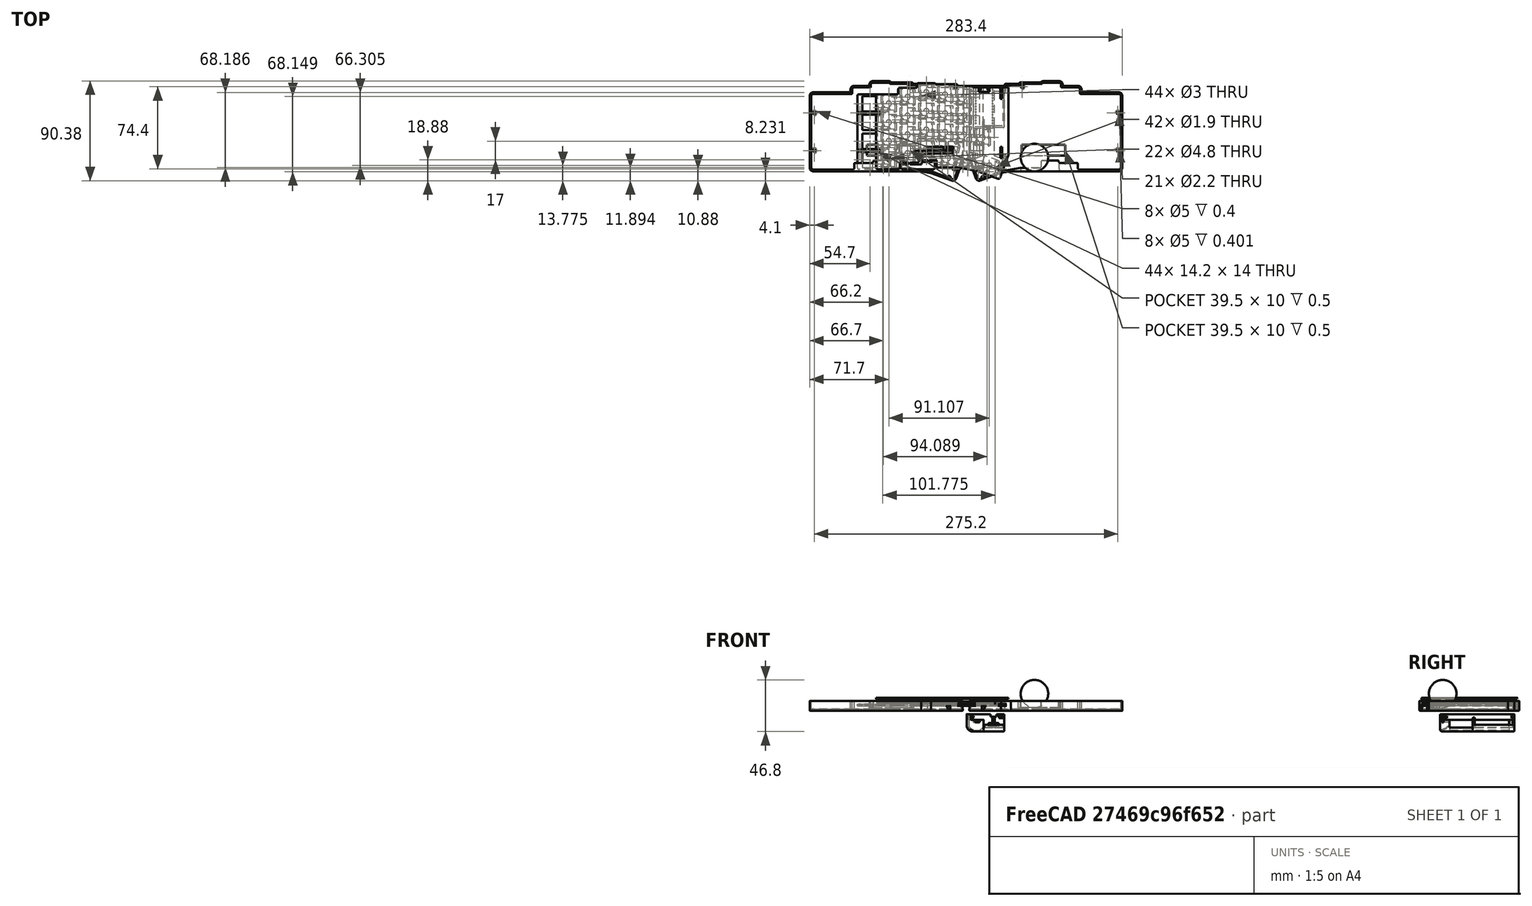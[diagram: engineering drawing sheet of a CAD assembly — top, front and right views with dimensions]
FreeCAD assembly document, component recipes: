
FREECAD ASSEMBLY — COMPONENT RECIPES ("simple-case-MS")

This assembly document has 5 components, labeled P0..P4 below (a component is one placed body or linked part). 4 of them carry a construction recipe — the FreeCAD feature program that regenerates the part from scratch, quoted from this document or its linked companion documents; the rest are supplied as boundary geometry only. No exploded tour is included for this assembly.
NOTE — this tour is split across 3 documents so each fits a 32k-token context. This is document 1: the component sections continue in the remaining 2 documents, each repeating the header above.
COMPONENT P0 — recipe-attached ("Body", modeled in this document).
Construction recipe (the document's own serialized feature program — sketch geometry with constraints, then the solid features built on it; lengths are millimeters unless a unit is written):

FEATURE [Sketcher::SketchObject] Sketch  label="xz"
  ArcFitTolerance = 0
  AttachmentSupport = -> [XZ_Plane]
  ExternalTypes = [0]
  FullyConstrained = false
  MakeInternals = false
  MapMode = 5
  Placement = pos=(0,0,0) rot=(1,0,0;1.5708rad)
  _ExternalGeoVersion = 0
  expr: Constraints[31] = Spreadsheet.conn_h
  expr: Constraints[57] = Spreadsheet.controller_h
  expr: Constraints[79] = Spreadsheet.battery_h
  sketch-geometry (55):
    g0: LineSegment [constr] StartX=9 StartY=2.5 StartZ=0 EndX=9 EndY=4.1 EndZ=0
    g1: LineSegment [constr] StartX=9 StartY=4.1 StartZ=0 EndX=-9 EndY=4.1 EndZ=0
    g2: LineSegment [constr] StartX=-9 StartY=4.1 StartZ=0 EndX=-9 EndY=2.5 EndZ=0
    g3: LineSegment [constr] StartX=-9 StartY=2.5 StartZ=0 EndX=9 EndY=2.5 EndZ=0
    g4: GeomPoint [constr] X=0 Y=3.3 Z=0
    g5: LineSegment [constr] StartX=-105.409 StartY=0 StartZ=0 EndX=45.7381 EndY=0 EndZ=0
    g6: LineSegment [constr] StartX=45.7381 StartY=0 StartZ=0 EndX=45.7381 EndY=-1.6 EndZ=0
    g7: LineSegment [constr] StartX=45.7381 StartY=-1.6 StartZ=0 EndX=-105.409 EndY=-1.6 EndZ=0
    g8: LineSegment [constr] StartX=-105.409 StartY=-1.6 StartZ=0 EndX=-105.409 EndY=0 EndZ=0
    g9: LineSegment [constr] StartX=9 StartY=2.5 StartZ=0 EndX=6.36312 EndY=2.5 EndZ=0
    g10: LineSegment [constr] StartX=6.36312 StartY=2.5 StartZ=0 EndX=6.36312 EndY=0 EndZ=0
    g11: LineSegment [constr] StartX=6.36312 StartY=0 StartZ=0 EndX=9 EndY=0 EndZ=0
    g12: LineSegment [constr] StartX=9 StartY=0 StartZ=0 EndX=9 EndY=2.5 EndZ=0
    g13: LineSegment [constr] StartX=4.55 StartY=-5.1 StartZ=0 EndX=4.55 EndY=-1.6 EndZ=0
    g14: LineSegment [constr] StartX=4.55 StartY=-1.6 StartZ=0 EndX=-4.55 EndY=-1.6 EndZ=0
    g15: LineSegment [constr] StartX=-4.55 StartY=-1.6 StartZ=0 EndX=-4.55 EndY=-5.1 EndZ=0
    g16: LineSegment [constr] StartX=-4.55 StartY=-5.1 StartZ=0 EndX=4.55 EndY=-5.1 EndZ=0
    g17: GeomPoint [constr] X=0 Y=-3.35 Z=0
    g18: LineSegment [constr] StartX=-4.75 StartY=6.3 StartZ=0 EndX=-4.75 EndY=4.1 EndZ=0
    g19: LineSegment [constr] StartX=-4.75 StartY=4.1 StartZ=0 EndX=4.75 EndY=4.1 EndZ=0
    g20: LineSegment [constr] StartX=4.75 StartY=4.1 StartZ=0 EndX=4.75 EndY=6.3 EndZ=0
    g21: LineSegment [constr] StartX=4.75 StartY=6.3 StartZ=0 EndX=-4.75 EndY=6.3 EndZ=0
    g22: GeomPoint [constr] X=0 Y=5.2 Z=0
    g23: LineSegment [constr] StartX=-44.4822 StartY=-5.1 StartZ=0 EndX=-44.4822 EndY=-3.9 EndZ=0
    g24: LineSegment [constr] StartX=-44.4822 StartY=-3.9 StartZ=0 EndX=44.4822 EndY=-3.9 EndZ=0
    g25: LineSegment [constr] StartX=44.4822 StartY=-3.9 StartZ=0 EndX=44.4822 EndY=-5.1 EndZ=0
    g26: LineSegment [constr] StartX=44.4822 StartY=-5.1 StartZ=0 EndX=-44.4822 EndY=-5.1 EndZ=0
    g27: GeomPoint [constr] X=0 Y=-4.5 Z=0
    g28: LineSegment [constr] StartX=-9.1 StartY=-3.6 StartZ=0 EndX=-9.1 EndY=9.4 EndZ=0
    g29: LineSegment [constr] StartX=-9.1 StartY=9.4 StartZ=0 EndX=-22.1 EndY=9.4 EndZ=0
    g30: LineSegment [constr] StartX=-22.1 StartY=9.4 StartZ=0 EndX=-22.1 EndY=-3.6 EndZ=0
    g31: LineSegment [constr] StartX=-22.1 StartY=-3.6 StartZ=0 EndX=-9.1 EndY=-3.6 EndZ=0
    g32: GeomPoint [constr] X=-15.6 Y=2.9 Z=0
    g33: LineSegment [constr] StartX=33.0788 StartY=0.6 StartZ=0 EndX=33.0788 EndY=2.2 EndZ=0
    g34: LineSegment [constr] StartX=33.0788 StartY=2.2 StartZ=0 EndX=11.9844 EndY=2.2 EndZ=0
    g35: LineSegment [constr] StartX=11.9844 StartY=2.2 StartZ=0 EndX=11.9844 EndY=0.6 EndZ=0
    g36: LineSegment [constr] StartX=11.9844 StartY=0.6 StartZ=0 EndX=33.0788 EndY=0.6 EndZ=0
    g37: GeomPoint [constr] X=22.5316 Y=1.4 Z=0
    g38: LineSegment [constr] StartX=25.7428 StartY=8.6 StartZ=0 EndX=25.7428 EndY=2.2 EndZ=0
    g39: LineSegment [constr] StartX=25.7428 StartY=2.2 StartZ=0 EndX=19.3204 EndY=2.2 EndZ=0
    g40: LineSegment [constr] StartX=19.3204 StartY=2.2 StartZ=0 EndX=19.3204 EndY=8.6 EndZ=0
    g41: LineSegment [constr] StartX=19.3204 StartY=8.6 StartZ=0 EndX=25.7428 EndY=8.6 EndZ=0
    g42: GeomPoint [constr] X=22.5316 Y=5.4 Z=0
    g43: LineSegment [constr] StartX=22.5316 StartY=1.4 StartZ=0 EndX=22.5316 EndY=5.4 EndZ=0
    g44: LineSegment [constr] StartX=29.8817 StartY=5.3 StartZ=0 EndX=29.8817 EndY=0 EndZ=0
    g45: LineSegment [constr] StartX=29.8817 StartY=0 StartZ=0 EndX=15.1815 EndY=0 EndZ=0
    g46: LineSegment [constr] StartX=15.1815 StartY=0 StartZ=0 EndX=15.1815 EndY=5.3 EndZ=0
    g47: LineSegment [constr] StartX=15.1815 StartY=5.3 StartZ=0 EndX=29.8817 EndY=5.3 EndZ=0
    g48: GeomPoint [constr] X=22.5316 Y=2.65 Z=0
    g49: LineSegment [constr] StartX=28.1684 StartY=6.59315 StartZ=0 EndX=28.1684 EndY=9.3 EndZ=0
    g50: LineSegment [constr] StartX=28.1684 StartY=9.3 StartZ=0 EndX=16.8947 EndY=9.3 EndZ=0
    g51: LineSegment [constr] StartX=16.8947 StartY=9.3 StartZ=0 EndX=16.8947 EndY=6.59315 EndZ=0
    g52: LineSegment [constr] StartX=16.8947 StartY=6.59315 StartZ=0 EndX=28.1684 EndY=6.59315 EndZ=0
    g53: GeomPoint [constr] X=22.5316 Y=7.94657 Z=0
    g54: Circle [constr] CenterX=41.3382 CenterY=8.9 CenterZ=0 NormalX=0 NormalY=0 NormalZ=1 AngleXU=0 Radius=12.5
  constraints (135):
    c: Coincident(g0,g1)
    c: Coincident(g1,g2)
    c: Coincident(g2,g3)
    c: Coincident(g3,g0)
    c: Horizontal(g1)
    c: Horizontal(g3)
    c: Vertical(g0)
    c: Vertical(g2)
    c: Symmetric(g1,g0,g4)
    c: PointOnObject(g4,g-2)
    c: Coincident(g5,g6)
    c: Coincident(g6,g7)
    c: Coincident(g7,g8)
    c: Coincident(g8,g5)
    c: Horizontal(g5)
    c: Horizontal(g7)
    c: Vertical(g6)
    c: Vertical(g8)
    c: PointOnObject(g5,g-1)
    c: Distance(g6) = 1.6
    c: Distance(g0) = 1.6
    c: Coincident(g9,g10)
    c: Coincident(g10,g11)
    c: Coincident(g11,g12)
    c: Coincident(g12,g9)
    c: Horizontal(g9)
    c: Horizontal(g11)
    c: Vertical(g10)
    c: Vertical(g12)
    c: Coincident(g9,g0)
    c: PointOnObject(g10,g5)
    c: Distance(g12) = 2.5
    c: Distance(g1) = 18
    c: Coincident(g13,g14)
    c: Coincident(g14,g15)
    c: Coincident(g15,g16)
    c: Coincident(g16,g13)
    c: Horizontal(g14)
    c: Horizontal(g16)
    c: Vertical(g13)
    c: Vertical(g15)
    c: Symmetric(g14,g13,g17)
    c: PointOnObject(g17,g-2)
    c: PointOnObject(g14,g7)
    c: Distance(g13) = 3.5
    c: Distance(g16) = 9.1
    c: Coincident(g18,g19)
    c: Coincident(g19,g20)
    c: Coincident(g20,g21)
    c: Coincident(g21,g18)
    c: Horizontal(g19)
    c: Horizontal(g21)
    c: Vertical(g18)
    c: Vertical(g20)
    c: Symmetric(g19,g18,g22)
    c: PointOnObject(g22,g-2)
    c: PointOnObject(g19,g1)
    c: Distance(g20,g3) = 3.8
    c: Distance(g21) = 9.5
    c: Coincident(g23,g24)
    c: Coincident(g24,g25)
    c: Coincident(g25,g26)
    c: Coincident(g26,g23)
    c: Horizontal(g24)
    c: Horizontal(g26)
    c: Vertical(g23)
    c: Vertical(g25)
    c: Symmetric(g24,g23,g27)
    c: PointOnObject(g27,g-2)
    c: Distance(g25) = 1.2
    c: Coincident(g28,g29)
    c: Coincident(g29,g30)
    c: Coincident(g30,g31)
    c: Coincident(g31,g28)
    c: Horizontal(g29)
    c: Horizontal(g31)
    c: Vertical(g28)
    c: Vertical(g30)
    c: Symmetric(g29,g28,g32)
    c: Distance(g30) = 13
    c: Distance(g29) = 13
    c: Distance(g30,g7) = 2
    c: Distance(g24,g7) = 2.3
    c: Distance(g32,g-2) = 15.6
    c: Coincident(g33,g34)
    c: Coincident(g34,g35)
    c: Coincident(g35,g36)
    c: Coincident(g36,g33)
    c: Horizontal(g34)
    c: Horizontal(g36)
    c: Vertical(g33)
    c: Vertical(g35)
    c: Symmetric(g34,g33,g37)
    c: Distance(g33) = 1.6
    c: Distance(g33,g5) = 0.6
    c: Coincident(g38,g39)
    c: Coincident(g39,g40)
    c: Coincident(g40,g41)
    c: Coincident(g41,g38)
    c: Horizontal(g39)
    c: Horizontal(g41)
    c: Vertical(g38)
    c: Vertical(g40)
    c: Symmetric(g39,g38,g42)
    c: PointOnObject(g39,g34)
    c: Distance(g40) = 6.4
    c: Coincident(g43,g37)
    c: Coincident(g43,g42)
    c: Vertical(g43)
    c: Coincident(g44,g45)
    c: Coincident(g45,g46)
    c: Coincident(g46,g47)
    c: Coincident(g47,g44)
    c: Horizontal(g45)
    c: Horizontal(g47)
    c: Vertical(g44)
    c: Vertical(g46)
    c: Symmetric(g45,g44,g48)
    c: PointOnObject(g48,g43)
    c: PointOnObject(g45,g5)
    c: Distance(g44) = 5.3
    c: Coincident(g49,g50)
    c: Coincident(g50,g51)
    c: Coincident(g51,g52)
    c: Coincident(g52,g49)
    c: Horizontal(g50)
    c: Horizontal(g52)
    c: Vertical(g49)
    c: Vertical(g51)
    c: Symmetric(g50,g49,g53)
    c: PointOnObject(g53,g43)
    c: Distance(g49,g47) = 4
    c: Diameter(g54) = 25
    c: Distance(g54,g24) = 12.8
    c: Distance(g33,g24) = 4.5
FEATURE [Sketcher::SketchObject] Sketch001  label="xy"
  ArcFitTolerance = 0
  AttachmentSupport = -> [XY_Plane]
  ExternalTypes = [0]
  FullyConstrained = true
  MakeInternals = false
  MapMode = 5
  _ExternalGeoVersion = 0
  expr: Constraints[23] = Spreadsheet.battery_l
  sketch-geometry (20):
    g0: LineSegment [constr] StartX=8.4 StartY=-34 StartZ=0 EndX=8.4 EndY=0 EndZ=0
    g1: LineSegment [constr] StartX=8.4 StartY=0 StartZ=0 EndX=-8.4 EndY=0 EndZ=0
    g2: LineSegment [constr] StartX=-8.4 StartY=0 StartZ=0 EndX=-8.4 EndY=-34 EndZ=0
    g3: LineSegment [constr] StartX=-8.4 StartY=-34 StartZ=0 EndX=8.4 EndY=-34 EndZ=0
    g4: GeomPoint [constr] X=0 Y=-17 Z=0
    g5: LineSegment [constr] StartX=-22.1 StartY=-60.7 StartZ=0 EndX=-22.1 EndY=-3.7 EndZ=0
    g6: LineSegment [constr] StartX=-22.1 StartY=-3.7 StartZ=0 EndX=-9.1 EndY=-3.7 EndZ=0
    g7: LineSegment [constr] StartX=-9.1 StartY=-3.7 StartZ=0 EndX=-9.1 EndY=-60.7 EndZ=0
    g8: LineSegment [constr] StartX=-9.1 StartY=-60.7 StartZ=0 EndX=-22.1 EndY=-60.7 EndZ=0
    g9: GeomPoint [constr] X=-15.6 Y=-32.2 Z=0
    g10: LineSegment [constr] StartX=22.1 StartY=-68.9 StartZ=0 EndX=22.1 EndY=0 EndZ=0
    g11: LineSegment [constr] StartX=22.1 StartY=0 StartZ=0 EndX=-22.1 EndY=0 EndZ=0
    g12: LineSegment [constr] StartX=-22.1 StartY=0 StartZ=0 EndX=-22.1 EndY=-68.9 EndZ=0
    g13: LineSegment [constr] StartX=-22.1 StartY=-68.9 StartZ=0 EndX=22.1 EndY=-68.9 EndZ=0
    g14: GeomPoint [constr] X=0 Y=-34.45 Z=0
    g15: LineSegment [constr] StartX=8.5 StartY=-53.9 StartZ=0 EndX=8.5 EndY=-36.9 EndZ=0
    g16: LineSegment [constr] StartX=8.5 StartY=-36.9 StartZ=0 EndX=-8.5 EndY=-36.9 EndZ=0
    g17: LineSegment [constr] StartX=-8.5 StartY=-36.9 StartZ=0 EndX=-8.5 EndY=-53.9 EndZ=0
    g18: LineSegment [constr] StartX=-8.5 StartY=-53.9 StartZ=0 EndX=8.5 EndY=-53.9 EndZ=0
    g19: GeomPoint [constr] X=0 Y=-45.4 Z=0
  constraints (52):
    c: Coincident(g0,g1)
    c: Coincident(g1,g2)
    c: Coincident(g2,g3)
    c: Coincident(g3,g0)
    c: Horizontal(g1)
    c: Horizontal(g3)
    c: Vertical(g0)
    c: Vertical(g2)
    c: Symmetric(g1,g0,g4)
    c: PointOnObject(g4,g-2)
    c: Distance(g0) = 34
    c: PointOnObject(g-1,g1)
    c: Distance(g3) = 16.8
    c: Coincident(g5,g6)
    c: Coincident(g6,g7)
    c: Coincident(g7,g8)
    c: Coincident(g8,g5)
    c: Horizontal(g6)
    c: Horizontal(g8)
    c: Vertical(g5)
    c: Vertical(g7)
    c: Symmetric(g6,g5,g9)
    c: Distance(g6) = 13
    c: Distance(g5) = 57
    c: Distance(g9,g-1) = 32.2
    c: Coincident(g10,g11)
    c: Coincident(g11,g12)
    c: Coincident(g12,g13)
    c: Coincident(g13,g10)
    c: Horizontal(g11)
    c: Horizontal(g13)
    c: Vertical(g10)
    c: Vertical(g12)
    c: Symmetric(g11,g10,g14)
    c: PointOnObject(g14,g-2)
    c: PointOnObject(g11,g-1)
    c: Distance(g12,g-2) = 22.1
    c: Distance(g10) = 68.9
    c: Coincident(g15,g16)
    c: Coincident(g16,g17)
    c: Coincident(g17,g18)
    c: Coincident(g18,g15)
    c: Horizontal(g16)
    c: Horizontal(g18)
    c: Vertical(g15)
    c: Vertical(g17)
    c: Symmetric(g16,g15,g19)
    c: PointOnObject(g19,g-2)
    c: Distance(g18) = 17
    c: Distance(g15) = 17
    c: Distance(g19,g-1) = 45.4
    c: Distance(g9,g-2) = 15.6
FEATURE [Sketcher::SketchObject] Sketch002
  ArcFitTolerance = 0
  AttachmentOffset = pos=(0,0,10.6) rot=(0,0,1;0rad)
  AttachmentSupport = -> [XY_Plane]
  ExternalTypes = [0]
  FullyConstrained = true
  MakeInternals = false
  MapMode = 5
  Placement = pos=(0,0,10.6) rot=(0,0,1;0rad)
  _ExternalGeoVersion = 0
  expr: .AttachmentOffset.Base.z = Spreadsheet.battery_h - 3.6 + 1.2
  expr: Constraints[10] = Sketch001.Constraints[10]
  expr: Constraints[12] = Sketch001.Constraints[12]
  expr: Constraints[22] = Sketch001.Constraints[22]
  expr: Constraints[23] = Sketch001.Constraints[23]
  expr: Constraints[24] = Sketch001.Constraints[24]
  expr: Constraints[36] = Sketch001.Constraints[36]
  expr: Constraints[37] = Sketch001.Constraints[37]
  expr: Constraints[48] = Sketch001.Constraints[48]
  expr: Constraints[49] = Sketch001.Constraints[49]
  expr: Constraints[50] = Sketch001.Constraints[50]
  expr: Constraints[51] = Sketch001.Constraints[51]
  sketch-geometry (37):
    g0: LineSegment [constr] StartX=8.4 StartY=-34 StartZ=0 EndX=8.4 EndY=0 EndZ=0
    g1: LineSegment [constr] StartX=8.4 StartY=0 StartZ=0 EndX=-8.4 EndY=0 EndZ=0
    g2: LineSegment [constr] StartX=-8.4 StartY=0 StartZ=0 EndX=-8.4 EndY=-34 EndZ=0
    g3: LineSegment [constr] StartX=-8.4 StartY=-34 StartZ=0 EndX=8.4 EndY=-34 EndZ=0
    g4: GeomPoint [constr] X=0 Y=-17 Z=0
    g5: LineSegment [constr] StartX=-22.1 StartY=-60.7 StartZ=0 EndX=-22.1 EndY=-3.7 EndZ=0
    g6: LineSegment [constr] StartX=-22.1 StartY=-3.7 StartZ=0 EndX=-9.1 EndY=-3.7 EndZ=0
    g7: LineSegment [constr] StartX=-9.1 StartY=-3.7 StartZ=0 EndX=-9.1 EndY=-60.7 EndZ=0
    g8: LineSegment [constr] StartX=-9.1 StartY=-60.7 StartZ=0 EndX=-22.1 EndY=-60.7 EndZ=0
    g9: GeomPoint [constr] X=-15.6 Y=-32.2 Z=0
    g10: LineSegment [constr] StartX=22.1 StartY=-68.9 StartZ=0 EndX=22.1 EndY=0 EndZ=0
    g11: LineSegment [constr] StartX=22.1 StartY=0 StartZ=0 EndX=-22.1 EndY=0 EndZ=0
    g12: LineSegment [constr] StartX=-22.1 StartY=0 StartZ=0 EndX=-22.1 EndY=-68.9 EndZ=0
    g13: LineSegment [constr] StartX=-22.1 StartY=-68.9 StartZ=0 EndX=22.1 EndY=-68.9 EndZ=0
    g14: GeomPoint [constr] X=0 Y=-34.45 Z=0
    g15: LineSegment [constr] StartX=8.5 StartY=-53.9 StartZ=0 EndX=8.5 EndY=-36.9 EndZ=0
    g16: LineSegment [constr] StartX=8.5 StartY=-36.9 StartZ=0 EndX=-8.5 EndY=-36.9 EndZ=0
    g17: LineSegment [constr] StartX=-8.5 StartY=-36.9 StartZ=0 EndX=-8.5 EndY=-53.9 EndZ=0
    g18: LineSegment [constr] StartX=-8.5 StartY=-53.9 StartZ=0 EndX=8.5 EndY=-53.9 EndZ=0
    g19: GeomPoint [constr] X=0 Y=-45.4 Z=0
    g20: LineSegment StartX=9.6 StartY=1.3 StartZ=0 EndX=-24.5 EndY=1.3 EndZ=0
    g21: LineSegment StartX=-24.5 StartY=1.3 StartZ=0 EndX=-24.5 EndY=-1.7 EndZ=0
    g22: LineSegment StartX=-24.5 StartY=-1.7 StartZ=0 EndX=-24.5 EndY=-1.7 EndZ=0
    g23: LineSegment StartX=-24.5 StartY=-1.7 StartZ=0 EndX=-24.5 EndY=-58.7602 EndZ=0
    g24: LineSegment [constr] StartX=-9.1 StartY=-61.6 StartZ=0 EndX=-9.1 EndY=-36.6 EndZ=0
    g25: LineSegment [constr] StartX=-21.7859 StartY=-66.2173 StartZ=0 EndX=-9.1 EndY=-61.6 EndZ=0
    g26: LineSegment StartX=-9.1 StartY=-36.6 StartZ=0 EndX=9.6 EndY=-36.6 EndZ=0
    g27: LineSegment StartX=9.6 StartY=-36.6 StartZ=0 EndX=9.6 EndY=1.3 EndZ=0
    g28: LineSegment StartX=-24.5 StartY=-58.7602 StartZ=0 EndX=-21.7859 EndY=-66.2173 EndZ=0
    g29: LineSegment [constr] StartX=26.9 StartY=-17.32 StartZ=0 EndX=26.9 EndY=-0.32 EndZ=0
    g30: LineSegment [constr] StartX=26.9 StartY=-0.32 StartZ=0 EndX=9.9 EndY=-0.32 EndZ=0
    g31: LineSegment [constr] StartX=9.9 StartY=-0.32 StartZ=0 EndX=9.9 EndY=-17.32 EndZ=0
    g32: LineSegment [constr] StartX=9.9 StartY=-17.32 StartZ=0 EndX=26.9 EndY=-17.32 EndZ=0
    g33: GeomPoint [constr] X=18.4 Y=-8.82 Z=0
    g34: LineSegment StartX=-9.1 StartY=-36.6 StartZ=0 EndX=-9.25 EndY=-36.6 EndZ=0
    g35: LineSegment StartX=-9.25 StartY=-36.6 StartZ=0 EndX=-9.25 EndY=-61.6546 EndZ=0
    g36: LineSegment StartX=-9.25 StartY=-61.6546 StartZ=0 EndX=-21.7859 EndY=-66.2173 EndZ=0
  constraints (100):
    c: Coincident(g0,g1)
    c: Coincident(g1,g2)
    c: Coincident(g2,g3)
    c: Coincident(g3,g0)
    c: Horizontal(g1)
    c: Horizontal(g3)
    c: Vertical(g0)
    c: Vertical(g2)
    c: Symmetric(g1,g0,g4)
    c: PointOnObject(g4,g-2)
    c: Distance(g0) = 34
    c: PointOnObject(g-1,g1)
    c: Distance(g3) = 16.8
    c: Coincident(g5,g6)
    c: Coincident(g6,g7)
    c: Coincident(g7,g8)
    c: Coincident(g8,g5)
    c: Horizontal(g6)
    c: Horizontal(g8)
    c: Vertical(g5)
    c: Vertical(g7)
    c: Symmetric(g6,g5,g9)
    c: Distance(g6) = 13
    c: Distance(g5) = 57
    c: Distance(g9,g-1) = 32.2
    c: Coincident(g10,g11)
    c: Coincident(g11,g12)
    c: Coincident(g12,g13)
    c: Coincident(g13,g10)
    c: Horizontal(g11)
    c: Horizontal(g13)
    c: Vertical(g10)
    c: Vertical(g12)
    c: Symmetric(g11,g10,g14)
    c: PointOnObject(g14,g-2)
    c: PointOnObject(g11,g-1)
    c: Distance(g12,g-2) = 22.1
    c: Distance(g10) = 68.9
    c: Coincident(g15,g16)
    c: Coincident(g16,g17)
    c: Coincident(g17,g18)
    c: Coincident(g18,g15)
    c: Horizontal(g16)
    c: Horizontal(g18)
    c: Vertical(g15)
    c: Vertical(g17)
    c: Symmetric(g16,g15,g19)
    c: PointOnObject(g19,g-2)
    c: Distance(g18) = 17
    c: Distance(g15) = 17
    c: Distance(g19,g-1) = 45.4
    c: Distance(g9,g-2) = 15.6
    c: Horizontal(g20)
    c: Coincident(g21,g20)
    c: Vertical(g21)
    c: Coincident(g22,g21)
    c: Horizontal(g22)
    c: Coincident(g23,g22)
    c: Vertical(g23)
    c: PointOnObject(g24,g7)
    c: Vertical(g24)
    c: Distance(g11,g21) = 2.4
    c: Distance(g21,g6) = 2
    c: Distance(g22,g5) = 2.4
    c: Coincident(g24,g25)
    c: Angle(g13,g25) = 0.349066
    c: DistanceY(g-1,g20) = 1.3
    c: Coincident(g26,g24)
    c: Horizontal(g26)
    c: Coincident(g27,g26)
    c: Coincident(g27,g20)
    c: Vertical(g27)
    c: Distance(g15,g26) = 0.3
    c: Coincident(g28,g23)
    c: Coincident(g28,g25)
    c: Distance(g25,g25) = 13.5
    c: Perpendicular(g28,g25)
    c: Distance(g24,g8) = 0.9
    c: Coincident(g29,g30)
    c: Coincident(g30,g31)
    c: Coincident(g31,g32)
    c: Coincident(g32,g29)
    c: Vertical(g29)
    c: Vertical(g31)
    c: Horizontal(g30)
    c: Horizontal(g32)
    c: Symmetric(g31,g29,g33)
    c: DistanceX(g30,g30) = 17
    c: DistanceY(g29,g29) = 17
    c: DistanceX(g-1,g33) = 18.4
    c: DistanceY(g33,g-1) = 8.82
    c: Distance(g31,g27) = 0.3
    c: Coincident(g24,g34)
    c: Horizontal(g34)
    c: Coincident(g34,g35)
    c: PointOnObject(g35,g25)
    c: Vertical(g35)
    c: Coincident(g35,g36)
    c: Coincident(g36,g25)
    c: Distance(g35,g7) = 0.15
FEATURE [PartDesign::Pad] Pad  label="ベース"
  Direction = (0,0,1)
  Length = 15.7
  Length2 = 10
  Profile = -> Sketch002
  ReferenceAxis = -> Sketch002 [N_Axis]
  Reversed = true
  SideType = 0
  Suppressed = false
  Type = 0
  Type2 = 0
  expr: Length = Spreadsheet.battery_h + 1.2 + 0.3 + 1.2
FEATURE [Sketcher::SketchObject] Sketch003
  ArcFitTolerance = 0
  AttachmentOffset = pos=(0,0,6.9) rot=(0,0,1;0rad)
  AttachmentSupport = -> [XY_Plane]
  ExternalTypes = [0]
  FullyConstrained = false
  MakeInternals = false
  MapMode = 5
  Placement = pos=(0,0,6.9) rot=(0,0,1;0rad)
  _ExternalGeoVersion = 0
  expr: .AttachmentOffset.Base.z = Spreadsheet.conn_h + Spreadsheet.controller_h + 0.6
  expr: Constraints[10] = Sketch001.Constraints[10]
  expr: Constraints[12] = Sketch001.Constraints[12]
  expr: Constraints[22] = Sketch001.Constraints[22]
  expr: Constraints[23] = Sketch001.Constraints[23]
  expr: Constraints[24] = Sketch001.Constraints[24]
  expr: Constraints[36] = Sketch001.Constraints[36]
  expr: Constraints[37] = Sketch001.Constraints[37]
  expr: Constraints[48] = Sketch001.Constraints[48]
  expr: Constraints[49] = Sketch001.Constraints[49]
  expr: Constraints[50] = Sketch001.Constraints[50]
  expr: Constraints[51] = Sketch001.Constraints[51]
  sketch-geometry (24):
    g0: LineSegment [constr] StartX=8.4 StartY=-34 StartZ=0 EndX=8.4 EndY=0 EndZ=0
    g1: LineSegment [constr] StartX=8.4 StartY=0 StartZ=0 EndX=-8.4 EndY=0 EndZ=0
    g2: LineSegment [constr] StartX=-8.4 StartY=0 StartZ=0 EndX=-8.4 EndY=-34 EndZ=0
    g3: LineSegment [constr] StartX=-8.4 StartY=-34 StartZ=0 EndX=8.4 EndY=-34 EndZ=0
    g4: GeomPoint [constr] X=0 Y=-17 Z=0
    g5: LineSegment [constr] StartX=-22.1 StartY=-60.7 StartZ=0 EndX=-22.1 EndY=-3.7 EndZ=0
    g6: LineSegment [constr] StartX=-22.1 StartY=-3.7 StartZ=0 EndX=-9.1 EndY=-3.7 EndZ=0
    g7: LineSegment [constr] StartX=-9.1 StartY=-3.7 StartZ=0 EndX=-9.1 EndY=-60.7 EndZ=0
    g8: LineSegment [constr] StartX=-9.1 StartY=-60.7 StartZ=0 EndX=-22.1 EndY=-60.7 EndZ=0
    g9: GeomPoint [constr] X=-15.6 Y=-32.2 Z=0
    g10: LineSegment [constr] StartX=22.1 StartY=-68.9 StartZ=0 EndX=22.1 EndY=0 EndZ=0
    g11: LineSegment [constr] StartX=22.1 StartY=0 StartZ=0 EndX=-22.1 EndY=0 EndZ=0
    g12: LineSegment [constr] StartX=-22.1 StartY=0 StartZ=0 EndX=-22.1 EndY=-68.9 EndZ=0
    g13: LineSegment [constr] StartX=-22.1 StartY=-68.9 StartZ=0 EndX=22.1 EndY=-68.9 EndZ=0
    g14: GeomPoint [constr] X=0 Y=-34.45 Z=0
    g15: LineSegment [constr] StartX=8.5 StartY=-53.9 StartZ=0 EndX=8.5 EndY=-36.9 EndZ=0
    g16: LineSegment [constr] StartX=8.5 StartY=-36.9 StartZ=0 EndX=-8.5 EndY=-36.9 EndZ=0
    g17: LineSegment [constr] StartX=-8.5 StartY=-36.9 StartZ=0 EndX=-8.5 EndY=-53.9 EndZ=0
    g18: LineSegment [constr] StartX=-8.5 StartY=-53.9 StartZ=0 EndX=8.5 EndY=-53.9 EndZ=0
    g19: GeomPoint [constr] X=0 Y=-45.4 Z=0
    g20: LineSegment StartX=8.4 StartY=0 StartZ=0 EndX=-9.1 EndY=0 EndZ=0
    g21: LineSegment StartX=-9.1 StartY=0 StartZ=0 EndX=-9.1 EndY=-40.6656 EndZ=0
    g22: LineSegment StartX=-9.1 StartY=-40.6656 StartZ=0 EndX=8.4 EndY=-40.6656 EndZ=0
    g23: LineSegment StartX=8.4 StartY=-40.6656 StartZ=0 EndX=8.4 EndY=0 EndZ=0
  constraints (62):
    c: Coincident(g0,g1)
    c: Coincident(g1,g2)
    c: Coincident(g2,g3)
    c: Coincident(g3,g0)
    c: Horizontal(g1)
    c: Horizontal(g3)
    c: Vertical(g0)
    c: Vertical(g2)
    c: Symmetric(g1,g0,g4)
    c: PointOnObject(g4,g-2)
    c: Distance(g0) = 34
    c: PointOnObject(g-1,g1)
    c: Distance(g3) = 16.8
    c: Coincident(g5,g6)
    c: Coincident(g6,g7)
    c: Coincident(g7,g8)
    c: Coincident(g8,g5)
    c: Horizontal(g6)
    c: Horizontal(g8)
    c: Vertical(g5)
    c: Vertical(g7)
    c: Symmetric(g6,g5,g9)
    c: Distance(g6) = 13
    c: Distance(g5) = 57
    c: Distance(g9,g-1) = 32.2
    c: Coincident(g10,g11)
    c: Coincident(g11,g12)
    c: Coincident(g12,g13)
    c: Coincident(g13,g10)
    c: Horizontal(g11)
    c: Horizontal(g13)
    c: Vertical(g10)
    c: Vertical(g12)
    c: Symmetric(g11,g10,g14)
    c: PointOnObject(g14,g-2)
    c: PointOnObject(g11,g-1)
    c: Distance(g12,g-2) = 22.1
    c: Distance(g10) = 68.9
    c: Coincident(g15,g16)
    c: Coincident(g16,g17)
    c: Coincident(g17,g18)
    c: Coincident(g18,g15)
    c: Horizontal(g16)
    c: Horizontal(g18)
    c: Vertical(g15)
    c: Vertical(g17)
    c: Symmetric(g16,g15,g19)
    c: PointOnObject(g19,g-2)
    c: Distance(g18) = 17
    c: Distance(g15) = 17
    c: Distance(g19,g-1) = 45.4
    c: Distance(g9,g-2) = 15.6
    c: Coincident(g20,g21)
    c: Coincident(g21,g22)
    c: Coincident(g22,g23)
    c: Coincident(g23,g20)
    c: Horizontal(g20)
    c: Horizontal(g22)
    c: Vertical(g21)
    c: Vertical(g23)
    c: Coincident(g20,g0)
    c: PointOnObject(g21,g7)
FEATURE [PartDesign::Pocket] Pocket  label="コントローラ部"
  BaseFeature = -> Pad
  Direction = (0,0,-1)
  Length = 5
  Length2 = 5
  Profile = -> Sketch003
  ReferenceAxis = -> Sketch003 [N_Axis]
  SideType = 0
  Suppressed = false
  Type = 1
  Type2 = 0
FEATURE [Sketcher::SketchObject] Sketch007
  ArcFitTolerance = 0
  AttachmentSupport = -> [XY_Plane]
  ExternalTypes = [0]
  FullyConstrained = false
  MakeInternals = false
  MapMode = 5
  _ExternalGeoVersion = 0
  expr: Constraints[10] = Sketch001.Constraints[10]
  expr: Constraints[12] = Sketch001.Constraints[12]
  expr: Constraints[21] = Sketch001.Constraints[22]
  expr: Constraints[22] = Sketch001.Constraints[23]
  expr: Constraints[23] = Sketch001.Constraints[24]
  expr: Constraints[35] = Sketch001.Constraints[36]
  expr: Constraints[36] = Sketch001.Constraints[37]
  expr: Constraints[47] = Sketch001.Constraints[48]
  expr: Constraints[48] = Sketch001.Constraints[49]
  expr: Constraints[49] = Sketch001.Constraints[50]
  expr: Constraints[50] = Sketch001.Constraints[51]
  sketch-geometry (28):
    g0: LineSegment [constr] StartX=8.4 StartY=-34 StartZ=0 EndX=8.4 EndY=0 EndZ=0
    g1: LineSegment [constr] StartX=8.4 StartY=0 StartZ=0 EndX=-8.4 EndY=0 EndZ=0
    g2: LineSegment [constr] StartX=-8.4 StartY=0 StartZ=0 EndX=-8.4 EndY=-34 EndZ=0
    g3: LineSegment [constr] StartX=-8.4 StartY=-34 StartZ=0 EndX=8.4 EndY=-34 EndZ=0
    g4: GeomPoint [constr] X=0 Y=-17 Z=0
    g5: LineSegment [constr] StartX=-22.1 StartY=-60.7 StartZ=0 EndX=-22.1 EndY=-3.7 EndZ=0
    g6: LineSegment [constr] StartX=-22.1 StartY=-3.7 StartZ=0 EndX=-9.1 EndY=-3.7 EndZ=0
    g7: LineSegment [constr] StartX=-9.1 StartY=-3.7 StartZ=0 EndX=-9.1 EndY=-60.7 EndZ=0
    g8: LineSegment [constr] StartX=-9.1 StartY=-60.7 StartZ=0 EndX=-22.1 EndY=-60.7 EndZ=0
    g9: GeomPoint [constr] X=-15.6 Y=-32.2 Z=0
    g10: LineSegment [constr] StartX=22.1 StartY=-68.9 StartZ=0 EndX=22.1 EndY=0 EndZ=0
    g11: LineSegment [constr] StartX=22.1 StartY=0 StartZ=0 EndX=-22.1 EndY=0 EndZ=0
    g12: LineSegment [constr] StartX=-22.1 StartY=0 StartZ=0 EndX=-22.1 EndY=-68.9 EndZ=0
    g13: LineSegment [constr] StartX=-22.1 StartY=-68.9 StartZ=0 EndX=22.1 EndY=-68.9 EndZ=0
    g14: GeomPoint [constr] X=0 Y=-34.45 Z=0
    g15: LineSegment [constr] StartX=8.5 StartY=-53.9 StartZ=0 EndX=8.5 EndY=-36.9 EndZ=0
    g16: LineSegment [constr] StartX=8.5 StartY=-36.9 StartZ=0 EndX=-8.5 EndY=-36.9 EndZ=0
    g17: LineSegment [constr] StartX=-8.5 StartY=-36.9 StartZ=0 EndX=-8.5 EndY=-53.9 EndZ=0
    g18: LineSegment [constr] StartX=-8.5 StartY=-53.9 StartZ=0 EndX=8.5 EndY=-53.9 EndZ=0
    g19: GeomPoint [constr] X=-1.4e-15 Y=-45.4 Z=0
    g20: LineSegment StartX=22.1 StartY=0 StartZ=0 EndX=-22.4 EndY=0 EndZ=0
    g21: LineSegment StartX=-22.4 StartY=0 StartZ=0 EndX=-22.4 EndY=-4 EndZ=0
    g22: LineSegment StartX=-22.4 StartY=-4 StartZ=0 EndX=-22.4 EndY=-60.9323 EndZ=0
    g23: LineSegment [constr] StartX=-22.4 StartY=-60.4 StartZ=0 EndX=-22.4 EndY=-68.9 EndZ=0
    g24: LineSegment [constr] StartX=-22.4 StartY=-68.9 StartZ=0 EndX=22.1 EndY=-68.9 EndZ=0
    g25: LineSegment StartX=22.1 StartY=-68.9 StartZ=0 EndX=22.1 EndY=0 EndZ=0
    g26: LineSegment StartX=-19.5 StartY=-68.9 StartZ=0 EndX=22.1 EndY=-68.9 EndZ=0
    g27: LineSegment StartX=-22.4 StartY=-60.9323 StartZ=0 EndX=-19.5 EndY=-68.9 EndZ=0
  constraints (71):
    c: Coincident(g0,g1)
    c: Coincident(g1,g2)
    c: Coincident(g2,g3)
    c: Coincident(g3,g0)
    c: Horizontal(g1)
    c: Horizontal(g3)
    c: Vertical(g0)
    c: Vertical(g2)
    c: Symmetric(g1,g0,g4)
    c: PointOnObject(g4,g-2)
    c: Distance(g0) = 34
    c: PointOnObject(g-1,g1)
    c: Distance(g3) = 16.8
    c: Coincident(g5,g6)
    c: Coincident(g6,g7)
    c: Coincident(g7,g8)
    c: Horizontal(g6)
    c: Horizontal(g8)
    c: Vertical(g5)
    c: Vertical(g7)
    c: Symmetric(g6,g5,g9)
    c: Distance(g6) = 13
    c: Distance(g5) = 57
    c: Distance(g9,g-1) = 32.2
    c: Coincident(g10,g11)
    c: Coincident(g11,g12)
    c: Coincident(g12,g13)
    c: Coincident(g13,g10)
    c: Horizontal(g11)
    c: Horizontal(g13)
    c: Vertical(g10)
    c: Vertical(g12)
    c: Symmetric(g11,g10,g14)
    c: PointOnObject(g14,g-2)
    c: PointOnObject(g11,g-1)
    c: Distance(g12,g-2) = 22.1
    c: Distance(g10) = 68.9
    c: Coincident(g15,g16)
    c: Coincident(g16,g17)
    c: Coincident(g17,g18)
    c: Coincident(g18,g15)
    c: Horizontal(g16)
    c: Horizontal(g18)
    c: Vertical(g15)
    c: Vertical(g17)
    c: Symmetric(g16,g15,g19)
    c: PointOnObject(g19,g-2)
    c: Distance(g18) = 17
    c: Distance(g15) = 17
    c: Distance(g19,g-1) = 45.4
    c: Distance(g9,g-2) = 15.6
    c: Coincident(g20,g10)
    c: PointOnObject(g20,g-1)
    c: Coincident(g21,g20)
    c: Vertical(g21)
    c: Vertical(g22)
    c: Vertical(g23)
    c: Coincident(g24,g23)
    c: Coincident(g24,g10)
    c: Horizontal(g24)
    c: Coincident(g25,g24)
    c: Coincident(g25,g20)
    c: Distance(g21,g12) = 0.3
    c: Distance(g21,g6) = 0.3
    c: PointOnObject(g26,g13)
    c: Coincident(g26,g10)
    c: Coincident(g27,g22)
    c: Coincident(g27,g26)
    c: Angle(g26,g27) = 1.91986
    c: DistanceX(g27,g27) = 2.9
    c: Coincident(g22,g21)
FEATURE [PartDesign::Pocket] Pocket001  label="基板部"
  BaseFeature = -> Pocket
  Direction = (0,0,-1)
  Length = 5
  Length2 = 5
  Profile = -> Sketch007
  ReferenceAxis = -> Sketch007 [N_Axis]
  SideType = 0
  Suppressed = false
  Type = 1
  Type2 = 0
FEATURE [Sketcher::SketchObject] Sketch008
  ArcFitTolerance = 0
  AttachmentOffset = pos=(0,0,3.4) rot=(0,0,1;0rad)
  AttachmentSupport = -> [XZ_Plane]
  ExternalTypes = [0]
  FullyConstrained = false
  MakeInternals = false
  MapMode = 5
  Placement = pos=(0,-3.4,8e-16) rot=(1,0,0;1.5708rad)
  _ExternalGeoVersion = 0
  expr: Constraints[105] = Sketch.Constraints[105]
  expr: Constraints[120] = Sketch.Constraints[120]
  expr: Constraints[131] = Sketch.Constraints[131]
  expr: Constraints[132] = Sketch.Constraints[132]
  expr: Constraints[133] = Sketch.Constraints[133]
  expr: Constraints[19] = Sketch.Constraints[19]
  expr: Constraints[20] = Sketch.Constraints[20]
  expr: Constraints[31] = Sketch.Constraints[31]
  expr: Constraints[32] = Sketch.Constraints[32]
  expr: Constraints[44] = Sketch.Constraints[44]
  expr: Constraints[45] = Sketch.Constraints[45]
  expr: Constraints[57] = Sketch.Constraints[57]
  expr: Constraints[58] = Sketch.Constraints[58]
  expr: Constraints[69] = Sketch.Constraints[69]
  expr: Constraints[79] = Sketch.Constraints[79]
  expr: Constraints[80] = Sketch.Constraints[80]
  expr: Constraints[81] = Sketch.Constraints[81]
  expr: Constraints[82] = Sketch.Constraints[82]
  expr: Constraints[83] = Sketch.Constraints[83]
  expr: Constraints[93] = Sketch.Constraints[93]
  expr: Constraints[94] = Sketch.Constraints[94]
  sketch-geometry (70):
    g0: LineSegment [constr] StartX=9 StartY=2.5 StartZ=0 EndX=9 EndY=4.1 EndZ=0
    g1: LineSegment [constr] StartX=9 StartY=4.1 StartZ=0 EndX=-9 EndY=4.1 EndZ=0
    g2: LineSegment [constr] StartX=-9 StartY=4.1 StartZ=0 EndX=-9 EndY=2.5 EndZ=0
    g3: LineSegment [constr] StartX=-9 StartY=2.5 StartZ=0 EndX=9 EndY=2.5 EndZ=0
    g4: GeomPoint [constr] X=0 Y=3.3 Z=0
    g5: LineSegment [constr] StartX=-105.409 StartY=0 StartZ=0 EndX=45.7381 EndY=0 EndZ=0
    g6: LineSegment [constr] StartX=45.7381 StartY=0 StartZ=0 EndX=45.7381 EndY=-1.6 EndZ=0
    g7: LineSegment [constr] StartX=45.7381 StartY=-1.6 StartZ=0 EndX=-105.409 EndY=-1.6 EndZ=0
    g8: LineSegment [constr] StartX=-105.409 StartY=-1.6 StartZ=0 EndX=-105.409 EndY=0 EndZ=0
    g9: LineSegment [constr] StartX=9 StartY=2.5 StartZ=0 EndX=6.36312 EndY=2.5 EndZ=0
    g10: LineSegment [constr] StartX=6.36312 StartY=2.5 StartZ=0 EndX=6.36312 EndY=0 EndZ=0
    g11: LineSegment [constr] StartX=6.36312 StartY=0 StartZ=0 EndX=9 EndY=0 EndZ=0
    g12: LineSegment [constr] StartX=9 StartY=0 StartZ=0 EndX=9 EndY=2.5 EndZ=0
    g13: LineSegment [constr] StartX=4.55 StartY=-5.1 StartZ=0 EndX=4.55 EndY=-1.6 EndZ=0
    g14: LineSegment [constr] StartX=4.55 StartY=-1.6 StartZ=0 EndX=-4.55 EndY=-1.6 EndZ=0
    g15: LineSegment [constr] StartX=-4.55 StartY=-1.6 StartZ=0 EndX=-4.55 EndY=-5.1 EndZ=0
    g16: LineSegment [constr] StartX=-4.55 StartY=-5.1 StartZ=0 EndX=4.55 EndY=-5.1 EndZ=0
    g17: GeomPoint [constr] X=0 Y=-3.35 Z=0
    g18: LineSegment [constr] StartX=-4.75 StartY=6.3 StartZ=0 EndX=-4.75 EndY=4.1 EndZ=0
    g19: LineSegment [constr] StartX=-4.75 StartY=4.1 StartZ=0 EndX=4.75 EndY=4.1 EndZ=0
    g20: LineSegment [constr] StartX=4.75 StartY=4.1 StartZ=0 EndX=4.75 EndY=6.3 EndZ=0
    g21: LineSegment [constr] StartX=4.75 StartY=6.3 StartZ=0 EndX=-4.75 EndY=6.3 EndZ=0
    g22: GeomPoint [constr] X=0 Y=5.2 Z=0
    g23: LineSegment [constr] StartX=-44.4822 StartY=-5.1 StartZ=0 EndX=-44.4822 EndY=-3.9 EndZ=0
    g24: LineSegment [constr] StartX=-44.4822 StartY=-3.9 StartZ=0 EndX=44.4822 EndY=-3.9 EndZ=0
    g25: LineSegment [constr] StartX=44.4822 StartY=-3.9 StartZ=0 EndX=44.4822 EndY=-5.1 EndZ=0
    g26: LineSegment [constr] StartX=44.4822 StartY=-5.1 StartZ=0 EndX=-44.4822 EndY=-5.1 EndZ=0
    g27: GeomPoint [constr] X=0 Y=-4.5 Z=0
    g28: LineSegment [constr] StartX=-9.1 StartY=-3.6 StartZ=0 EndX=-9.1 EndY=9.4 EndZ=0
    g29: LineSegment [constr] StartX=-9.1 StartY=9.4 StartZ=0 EndX=-22.1 EndY=9.4 EndZ=0
    g30: LineSegment [constr] StartX=-22.1 StartY=9.4 StartZ=0 EndX=-22.1 EndY=-3.6 EndZ=0
    g31: LineSegment [constr] StartX=-22.1 StartY=-3.6 StartZ=0 EndX=-9.1 EndY=-3.6 EndZ=0
    g32: GeomPoint [constr] X=-15.6 Y=2.9 Z=0
    g33: LineSegment [constr] StartX=33.0788 StartY=0.6 StartZ=0 EndX=33.0788 EndY=2.2 EndZ=0
    g34: LineSegment [constr] StartX=33.0788 StartY=2.2 StartZ=0 EndX=11.9844 EndY=2.2 EndZ=0
    g35: LineSegment [constr] StartX=11.9844 StartY=2.2 StartZ=0 EndX=11.9844 EndY=0.6 EndZ=0
    g36: LineSegment [constr] StartX=11.9844 StartY=0.6 StartZ=0 EndX=33.0788 EndY=0.6 EndZ=0
    g37: GeomPoint [constr] X=22.5316 Y=1.4 Z=0
    g38: LineSegment [constr] StartX=25.7428 StartY=8.6 StartZ=0 EndX=25.7428 EndY=2.2 EndZ=0
    g39: LineSegment [constr] StartX=25.7428 StartY=2.2 StartZ=0 EndX=19.3204 EndY=2.2 EndZ=0
    g40: LineSegment [constr] StartX=19.3204 StartY=2.2 StartZ=0 EndX=19.3204 EndY=8.6 EndZ=0
    g41: LineSegment [constr] StartX=19.3204 StartY=8.6 StartZ=0 EndX=25.7428 EndY=8.6 EndZ=0
    g42: GeomPoint [constr] X=22.5316 Y=5.4 Z=0
    g43: LineSegment [constr] StartX=22.5316 StartY=1.4 StartZ=0 EndX=22.5316 EndY=5.4 EndZ=0
    g44: LineSegment [constr] StartX=29.8817 StartY=5.3 StartZ=0 EndX=29.8817 EndY=0 EndZ=0
    g45: LineSegment [constr] StartX=29.8817 StartY=0 StartZ=0 EndX=15.1815 EndY=0 EndZ=0
    g46: LineSegment [constr] StartX=15.1815 StartY=0 StartZ=0 EndX=15.1815 EndY=5.3 EndZ=0
    g47: LineSegment [constr] StartX=15.1815 StartY=5.3 StartZ=0 EndX=29.8817 EndY=5.3 EndZ=0
    g48: GeomPoint [constr] X=22.5316 Y=2.65 Z=0
    g49: LineSegment [constr] StartX=28.1684 StartY=6.59315 StartZ=0 EndX=28.1684 EndY=9.3 EndZ=0
    g50: LineSegment [constr] StartX=28.1684 StartY=9.3 StartZ=0 EndX=16.8947 EndY=9.3 EndZ=0
    g51: LineSegment [constr] StartX=16.8947 StartY=9.3 StartZ=0 EndX=16.8947 EndY=6.59315 EndZ=0
    g52: LineSegment [constr] StartX=16.8947 StartY=6.59315 StartZ=0 EndX=28.1684 EndY=6.59315 EndZ=0
    g53: GeomPoint [constr] X=22.5316 Y=7.94657 Z=0
    g54: Circle [constr] CenterX=41.3382 CenterY=8.9 CenterZ=0 NormalX=0 NormalY=0 NormalZ=1 AngleXU=0 Radius=12.5
    g55: GeomPoint [constr] X=-15.6 Y=2.9 Z=0
    g56: LineSegment [constr] StartX=-15.6 StartY=2.9 StartZ=0 EndX=-15.6 EndY=9.4 EndZ=0
    g57: Circle [constr] CenterX=-15.6 CenterY=2.9 CenterZ=0 NormalX=0 NormalY=0 NormalZ=1 AngleXU=0 Radius=6.5
    g58: LineSegment [constr] StartX=-26.7128 StartY=2.9 StartZ=0 EndX=-11.1456 EndY=2.9 EndZ=0
    g59: ArcOfCircle [constr] CenterX=-15.6 CenterY=2.9 CenterZ=0 NormalX=0 NormalY=0 NormalZ=1 AngleXU=0 Radius=7 StartAngle=0 EndAngle=3.14159
    g60: LineSegment [constr] StartX=-21.3446 StartY=6.9 StartZ=0 EndX=-9.85544 EndY=6.9 EndZ=0
    g61: LineSegment [constr] StartX=-18.1981 StartY=9.4 StartZ=0 EndX=-13.0019 EndY=9.4 EndZ=0
    g62: ArcOfCircle CenterX=-15.6 CenterY=2.9 CenterZ=0 NormalX=0 NormalY=0 NormalZ=1 AngleXU=0 Radius=7 StartAngle=0.608246 EndAngle=1.19055
    g63: ArcOfCircle CenterX=-15.6 CenterY=2.9 CenterZ=0 NormalX=0 NormalY=0 NormalZ=1 AngleXU=0 Radius=7 StartAngle=1.95105 EndAngle=2.53335
    g64: LineSegment StartX=-18.1981 StartY=9.4 StartZ=0 EndX=-13.0019 EndY=9.4 EndZ=0
    g65: LineSegment StartX=-21.3446 StartY=6.9 StartZ=0 EndX=-22.1 EndY=6.9 EndZ=0
    g66: LineSegment StartX=-22.1 StartY=6.9 StartZ=0 EndX=-22.1 EndY=-3.6 EndZ=0
    g67: LineSegment StartX=-22.1 StartY=-3.6 StartZ=0 EndX=-9.1 EndY=-3.6 EndZ=0
    g68: LineSegment StartX=-9.85544 StartY=6.9 StartZ=0 EndX=-9.1 EndY=6.9 EndZ=0
    g69: LineSegment StartX=-9.1 StartY=6.9 StartZ=0 EndX=-9.1 EndY=-3.6 EndZ=0
  constraints (176):
    c: Coincident(g0,g1)
    c: Coincident(g1,g2)
    c: Coincident(g2,g3)
    c: Coincident(g3,g0)
    c: Horizontal(g1)
    c: Horizontal(g3)
    c: Vertical(g0)
    c: Vertical(g2)
    c: Symmetric(g1,g0,g4)
    c: PointOnObject(g4,g-2)
    c: Coincident(g5,g6)
    c: Coincident(g6,g7)
    c: Coincident(g7,g8)
    c: Coincident(g8,g5)
    c: Horizontal(g5)
    c: Horizontal(g7)
    c: Vertical(g6)
    c: Vertical(g8)
    c: PointOnObject(g5,g-1)
    c: Distance(g6) = 1.6
    c: Distance(g0) = 1.6
    c: Coincident(g9,g10)
    c: Coincident(g10,g11)
    c: Coincident(g11,g12)
    c: Coincident(g12,g9)
    c: Horizontal(g9)
    c: Horizontal(g11)
    c: Vertical(g10)
    c: Vertical(g12)
    c: Coincident(g9,g0)
    c: PointOnObject(g10,g5)
    c: Distance(g12) = 2.5
    c: Distance(g1) = 18
    c: Coincident(g13,g14)
    c: Coincident(g14,g15)
    c: Coincident(g15,g16)
    c: Coincident(g16,g13)
    c: Horizontal(g14)
    c: Horizontal(g16)
    c: Vertical(g13)
    c: Vertical(g15)
    c: Symmetric(g14,g13,g17)
    c: PointOnObject(g17,g-2)
    c: PointOnObject(g14,g7)
    c: Distance(g13) = 3.5
    c: Distance(g16) = 9.1
    c: Coincident(g18,g19)
    c: Coincident(g19,g20)
    c: Coincident(g20,g21)
    c: Coincident(g21,g18)
    c: Horizontal(g19)
    c: Horizontal(g21)
    c: Vertical(g18)
    c: Vertical(g20)
    c: Symmetric(g19,g18,g22)
    c: PointOnObject(g22,g-2)
    c: PointOnObject(g19,g1)
    c: Distance(g20,g3) = 3.8
    c: Distance(g21) = 9.5
    c: Coincident(g23,g24)
    c: Coincident(g24,g25)
    c: Coincident(g25,g26)
    c: Coincident(g26,g23)
    c: Horizontal(g24)
    c: Horizontal(g26)
    c: Vertical(g23)
    c: Vertical(g25)
    c: Symmetric(g24,g23,g27)
    c: PointOnObject(g27,g-2)
    c: Distance(g25) = 1.2
    c: Coincident(g28,g29)
    c: Coincident(g29,g30)
    c: Coincident(g30,g31)
    c: Coincident(g31,g28)
    c: Horizontal(g29)
    c: Horizontal(g31)
    c: Vertical(g28)
    c: Vertical(g30)
    c: Symmetric(g29,g28,g32)
    c: Distance(g30) = 13
    c: Distance(g29) = 13
    c: Distance(g30,g7) = 2
    c: Distance(g24,g7) = 2.3
    c: Distance(g32,g-2) = 15.6
    c: Coincident(g33,g34)
    c: Coincident(g34,g35)
    c: Coincident(g35,g36)
    c: Coincident(g36,g33)
    c: Horizontal(g34)
    c: Horizontal(g36)
    c: Vertical(g33)
    c: Vertical(g35)
    c: Symmetric(g34,g33,g37)
    c: Distance(g33) = 1.6
    c: Distance(g33,g5) = 0.6
    c: Coincident(g38,g39)
    c: Coincident(g39,g40)
    c: Coincident(g40,g41)
    c: Coincident(g41,g38)
    c: Horizontal(g39)
    c: Horizontal(g41)
    c: Vertical(g38)
    c: Vertical(g40)
    c: Symmetric(g39,g38,g42)
    c: PointOnObject(g39,g34)
    c: Distance(g40) = 6.4
    c: Coincident(g43,g37)
    c: Coincident(g43,g42)
    c: Vertical(g43)
    c: Coincident(g44,g45)
    c: Coincident(g45,g46)
    c: Coincident(g46,g47)
    c: Coincident(g47,g44)
    c: Horizontal(g45)
    c: Horizontal(g47)
    c: Vertical(g44)
    c: Vertical(g46)
    c: Symmetric(g45,g44,g48)
    c: PointOnObject(g48,g43)
    c: PointOnObject(g45,g5)
    c: Distance(g44) = 5.3
    c: Coincident(g49,g50)
    c: Coincident(g50,g51)
    c: Coincident(g51,g52)
    c: Coincident(g52,g49)
    c: Horizontal(g50)
    c: Horizontal(g52)
    c: Vertical(g49)
    c: Vertical(g51)
    c: Symmetric(g50,g49,g53)
    c: PointOnObject(g53,g43)
    c: Distance(g49,g47) = 4
    c: Diameter(g54) = 25
    c: Distance(g54,g24) = 12.8
    c: Distance(g33,g24) = 4.5
    c: Coincident(g55,g32)
    c: Coincident(g56,g32)
    c: PointOnObject(g56,g29)
    c: Vertical(g56)
    c: PointOnObject(g57,g56)
    c: PointOnObject(g56,g57)
    c: Diameter(g57) = 13
    c: Horizontal(g58)
    c: PointOnObject(g57,g58)
    c: Coincident(g59,g57)
    c: PointOnObject(g59,g58)
    c: PointOnObject(g59,g58)
    c: Radius(g59) = 7
    c: PointOnObject(g60,g59)
    c: PointOnObject(g60,g59)
    c: Horizontal(g60)
    c: Distance(g56,g60) = 2.5
    c: PointOnObject(g61,g29)
    c: PointOnObject(g61,g29)
    c: Coincident(g62,g57)
    c: Coincident(g62,g60)
    c: Coincident(g62,g61)
    c: Coincident(g63,g62)
    c: Coincident(g63,g61)
    c: Coincident(g63,g60)
    c: Coincident(g64,g63)
    c: Coincident(g64,g62)
    c: Coincident(g65,g63)
    c: Horizontal(g65)
    c: Coincident(g66,g65)
    c: PointOnObject(g66,g31)
    c: Vertical(g66)
    c: Coincident(g67,g66)
    c: PointOnObject(g67,g31)
    c: Coincident(g68,g62)
    c: Horizontal(g68)
    c: Coincident(g69,g68)
    c: Coincident(g69,g67)
    c: Vertical(g69)
    c: PointOnObject(g65,g30)
    c: PointOnObject(g68,g28)
FEATURE [Sketcher::SketchObject] Sketch011
  ArcFitTolerance = 0
  AttachmentSupport = -> [XZ_Plane]
  ExternalTypes = [0]
  FullyConstrained = false
  MakeInternals = false
  MapMode = 5
  Placement = pos=(0,0,0) rot=(1,0,0;1.5708rad)
  _ExternalGeoVersion = 0
  expr: Constraints[105] = Sketch.Constraints[105]
  expr: Constraints[120] = Sketch.Constraints[120]
  expr: Constraints[131] = Sketch.Constraints[131]
  expr: Constraints[132] = Sketch.Constraints[132]
  expr: Constraints[133] = Sketch.Constraints[133]
  expr: Constraints[19] = Sketch.Constraints[19]
  expr: Constraints[20] = Sketch.Constraints[20]
  expr: Constraints[31] = Sketch.Constraints[31]
  expr: Constraints[32] = Sketch.Constraints[32]
  expr: Constraints[44] = Sketch.Constraints[44]
  expr: Constraints[45] = Sketch.Constraints[45]
  expr: Constraints[57] = Sketch.Constraints[57]
  expr: Constraints[58] = Sketch.Constraints[58]
  expr: Constraints[69] = Sketch.Constraints[69]
  expr: Constraints[79] = Sketch.Constraints[79]
  expr: Constraints[80] = Sketch.Constraints[80]
  expr: Constraints[81] = Sketch.Constraints[81]
  expr: Constraints[82] = Sketch.Constraints[82]
  expr: Constraints[83] = Sketch.Constraints[83]
  expr: Constraints[93] = Sketch.Constraints[93]
  expr: Constraints[94] = Sketch.Constraints[94]
  sketch-geometry (73):
    g0: LineSegment [constr] StartX=9 StartY=2.5 StartZ=0 EndX=9 EndY=4.1 EndZ=0
    g1: LineSegment [constr] StartX=9 StartY=4.1 StartZ=0 EndX=-9 EndY=4.1 EndZ=0
    g2: LineSegment [constr] StartX=-9 StartY=4.1 StartZ=0 EndX=-9 EndY=2.5 EndZ=0
    g3: LineSegment [constr] StartX=-9 StartY=2.5 StartZ=0 EndX=9 EndY=2.5 EndZ=0
    g4: GeomPoint [constr] X=0 Y=3.3 Z=0
    g5: LineSegment [constr] StartX=-105.409 StartY=0 StartZ=0 EndX=45.7381 EndY=0 EndZ=0
    g6: LineSegment [constr] StartX=45.7381 StartY=0 StartZ=0 EndX=45.7381 EndY=-1.6 EndZ=0
    g7: LineSegment [constr] StartX=45.7381 StartY=-1.6 StartZ=0 EndX=-105.409 EndY=-1.6 EndZ=0
    g8: LineSegment [constr] StartX=-105.409 StartY=-1.6 StartZ=0 EndX=-105.409 EndY=0 EndZ=0
    g9: LineSegment [constr] StartX=9 StartY=2.5 StartZ=0 EndX=6.36312 EndY=2.5 EndZ=0
    g10: LineSegment [constr] StartX=6.36312 StartY=2.5 StartZ=0 EndX=6.36312 EndY=0 EndZ=0
    g11: LineSegment [constr] StartX=6.36312 StartY=0 StartZ=0 EndX=9 EndY=0 EndZ=0
    g12: LineSegment [constr] StartX=9 StartY=0 StartZ=0 EndX=9 EndY=2.5 EndZ=0
    g13: LineSegment [constr] StartX=4.55 StartY=-5.1 StartZ=0 EndX=4.55 EndY=-1.6 EndZ=0
    g14: LineSegment [constr] StartX=4.55 StartY=-1.6 StartZ=0 EndX=-4.55 EndY=-1.6 EndZ=0
    g15: LineSegment [constr] StartX=-4.55 StartY=-1.6 StartZ=0 EndX=-4.55 EndY=-5.1 EndZ=0
    g16: LineSegment [constr] StartX=-4.55 StartY=-5.1 StartZ=0 EndX=4.55 EndY=-5.1 EndZ=0
    g17: GeomPoint [constr] X=0 Y=-3.35 Z=0
    g18: LineSegment [constr] StartX=-4.75 StartY=6.3 StartZ=0 EndX=-4.75 EndY=4.1 EndZ=0
    g19: LineSegment [constr] StartX=-4.75 StartY=4.1 StartZ=0 EndX=4.75 EndY=4.1 EndZ=0
    g20: LineSegment [constr] StartX=4.75 StartY=4.1 StartZ=0 EndX=4.75 EndY=6.3 EndZ=0
    g21: LineSegment [constr] StartX=4.75 StartY=6.3 StartZ=0 EndX=-4.75 EndY=6.3 EndZ=0
    g22: GeomPoint [constr] X=0 Y=5.2 Z=0
    g23: LineSegment [constr] StartX=-44.4822 StartY=-5.1 StartZ=0 EndX=-44.4822 EndY=-3.9 EndZ=0
    g24: LineSegment [constr] StartX=-44.4822 StartY=-3.9 StartZ=0 EndX=44.4822 EndY=-3.9 EndZ=0
    g25: LineSegment [constr] StartX=44.4822 StartY=-3.9 StartZ=0 EndX=44.4822 EndY=-5.1 EndZ=0
    g26: LineSegment [constr] StartX=44.4822 StartY=-5.1 StartZ=0 EndX=-44.4822 EndY=-5.1 EndZ=0
    g27: GeomPoint [constr] X=0 Y=-4.5 Z=0
    g28: LineSegment [constr] StartX=-9.1 StartY=-3.6 StartZ=0 EndX=-9.1 EndY=9.4 EndZ=0
    g29: LineSegment [constr] StartX=-9.1 StartY=9.4 StartZ=0 EndX=-22.1 EndY=9.4 EndZ=0
    g30: LineSegment [constr] StartX=-22.1 StartY=9.4 StartZ=0 EndX=-22.1 EndY=-3.6 EndZ=0
    g31: LineSegment [constr] StartX=-22.1 StartY=-3.6 StartZ=0 EndX=-9.1 EndY=-3.6 EndZ=0
    g32: GeomPoint [constr] X=-15.6 Y=2.9 Z=0
    g33: LineSegment [constr] StartX=33.0788 StartY=0.6 StartZ=0 EndX=33.0788 EndY=2.2 EndZ=0
    g34: LineSegment [constr] StartX=33.0788 StartY=2.2 StartZ=0 EndX=11.9844 EndY=2.2 EndZ=0
    g35: LineSegment [constr] StartX=11.9844 StartY=2.2 StartZ=0 EndX=11.9844 EndY=0.6 EndZ=0
    g36: LineSegment [constr] StartX=11.9844 StartY=0.6 StartZ=0 EndX=33.0788 EndY=0.6 EndZ=0
    g37: GeomPoint [constr] X=22.5316 Y=1.4 Z=0
    g38: LineSegment [constr] StartX=25.7428 StartY=8.6 StartZ=0 EndX=25.7428 EndY=2.2 EndZ=0
    g39: LineSegment [constr] StartX=25.7428 StartY=2.2 StartZ=0 EndX=19.3204 EndY=2.2 EndZ=0
    g40: LineSegment [constr] StartX=19.3204 StartY=2.2 StartZ=0 EndX=19.3204 EndY=8.6 EndZ=0
    g41: LineSegment [constr] StartX=19.3204 StartY=8.6 StartZ=0 EndX=25.7428 EndY=8.6 EndZ=0
    g42: GeomPoint [constr] X=22.5316 Y=5.4 Z=0
    g43: LineSegment [constr] StartX=22.5316 StartY=1.4 StartZ=0 EndX=22.5316 EndY=5.4 EndZ=0
    g44: LineSegment [constr] StartX=29.8817 StartY=5.3 StartZ=0 EndX=29.8817 EndY=0 EndZ=0
    g45: LineSegment [constr] StartX=29.8817 StartY=0 StartZ=0 EndX=15.1815 EndY=0 EndZ=0
    g46: LineSegment [constr] StartX=15.1815 StartY=0 StartZ=0 EndX=15.1815 EndY=5.3 EndZ=0
    g47: LineSegment [constr] StartX=15.1815 StartY=5.3 StartZ=0 EndX=29.8817 EndY=5.3 EndZ=0
    g48: GeomPoint [constr] X=22.5316 Y=2.65 Z=0
    g49: LineSegment [constr] StartX=28.1684 StartY=6.59315 StartZ=0 EndX=28.1684 EndY=9.3 EndZ=0
    g50: LineSegment [constr] StartX=28.1684 StartY=9.3 StartZ=0 EndX=16.8947 EndY=9.3 EndZ=0
    g51: LineSegment [constr] StartX=16.8947 StartY=9.3 StartZ=0 EndX=16.8947 EndY=6.59315 EndZ=0
    g52: LineSegment [constr] StartX=16.8947 StartY=6.59315 StartZ=0 EndX=28.1684 EndY=6.59315 EndZ=0
    g53: GeomPoint [constr] X=22.5316 Y=7.94657 Z=0
    g54: Circle [constr] CenterX=41.3382 CenterY=8.9 CenterZ=0 NormalX=0 NormalY=0 NormalZ=1 AngleXU=0 Radius=12.5
    g55: LineSegment StartX=2.65 StartY=-2.8 StartZ=0 EndX=2.65 EndY=-5.1 EndZ=0
    g56: LineSegment StartX=2.65 StartY=-5.1 StartZ=0 EndX=-2.65 EndY=-5.1 EndZ=0
    g57: LineSegment StartX=-2.65 StartY=-5.1 StartZ=0 EndX=-2.65 EndY=-2.8 EndZ=0
    g58: LineSegment StartX=-2.65 StartY=-2.8 StartZ=0 EndX=2.65 EndY=-2.8 EndZ=0
    g59: GeomPoint [constr] X=0 Y=-3.95 Z=0
    g60: LineSegment StartX=-4.65 StartY=3.35 StartZ=0 EndX=-4.65 EndY=5.65 EndZ=0
    g61: LineSegment StartX=-4.15 StartY=6.15 StartZ=0 EndX=4.15 EndY=6.15 EndZ=0
    g62: LineSegment StartX=4.65 StartY=5.65 StartZ=0 EndX=4.65 EndY=3.35 EndZ=0
    g63: LineSegment StartX=4.15 StartY=2.85 StartZ=0 EndX=-4.15 EndY=2.85 EndZ=0
    g64: GeomPoint [constr] X=0 Y=4.5 Z=0
    g65: ArcOfCircle CenterX=-4.15 CenterY=5.65 CenterZ=0 NormalX=0 NormalY=0 NormalZ=1 AngleXU=0 Radius=0.5 StartAngle=1.5708 EndAngle=3.14159
    g66: GeomPoint [constr] X=-4.65 Y=6.15 Z=0
    g67: ArcOfCircle CenterX=-4.15 CenterY=3.35 CenterZ=0 NormalX=0 NormalY=0 NormalZ=1 AngleXU=0 Radius=0.5 StartAngle=3.14159 EndAngle=4.71239
    g68: GeomPoint [constr] X=-4.65 Y=2.85 Z=0
    g69: ArcOfCircle CenterX=4.15 CenterY=3.35 CenterZ=0 NormalX=0 NormalY=0 NormalZ=1 AngleXU=0 Radius=0.5 StartAngle=4.71239 EndAngle=6.28319
    g70: GeomPoint [constr] X=4.65 Y=2.85 Z=0
    g71: ArcOfCircle CenterX=4.15 CenterY=5.65 CenterZ=0 NormalX=0 NormalY=0 NormalZ=1 AngleXU=0 Radius=0.5 StartAngle=0 EndAngle=1.5708
    g72: GeomPoint [constr] X=4.65 Y=6.15 Z=0
  constraints (177):
    c: Coincident(g0,g1)
    c: Coincident(g1,g2)
    c: Coincident(g2,g3)
    c: Coincident(g3,g0)
    c: Horizontal(g1)
    c: Horizontal(g3)
    c: Vertical(g0)
    c: Vertical(g2)
    c: Symmetric(g1,g0,g4)
    c: PointOnObject(g4,g-2)
    c: Coincident(g5,g6)
    c: Coincident(g6,g7)
    c: Coincident(g7,g8)
    c: Coincident(g8,g5)
    c: Horizontal(g5)
    c: Horizontal(g7)
    c: Vertical(g6)
    c: Vertical(g8)
    c: PointOnObject(g5,g-1)
    c: Distance(g6) = 1.6
    c: Distance(g0) = 1.6
    c: Coincident(g9,g10)
    c: Coincident(g10,g11)
    c: Coincident(g11,g12)
    c: Coincident(g12,g9)
    c: Horizontal(g9)
    c: Horizontal(g11)
    c: Vertical(g10)
    c: Vertical(g12)
    c: Coincident(g9,g0)
    c: PointOnObject(g10,g5)
    c: Distance(g12) = 2.5
    c: Distance(g1) = 18
    c: Coincident(g13,g14)
    c: Coincident(g14,g15)
    c: Coincident(g15,g16)
    c: Coincident(g16,g13)
    c: Horizontal(g14)
    c: Horizontal(g16)
    c: Vertical(g13)
    c: Vertical(g15)
    c: Symmetric(g14,g13,g17)
    c: PointOnObject(g17,g-2)
    c: PointOnObject(g14,g7)
    c: Distance(g13) = 3.5
    c: Distance(g16) = 9.1
    c: Coincident(g18,g19)
    c: Coincident(g19,g20)
    c: Coincident(g20,g21)
    c: Coincident(g21,g18)
    c: Horizontal(g19)
    c: Horizontal(g21)
    c: Vertical(g18)
    c: Vertical(g20)
    c: Symmetric(g19,g18,g22)
    c: PointOnObject(g22,g-2)
    c: PointOnObject(g19,g1)
    c: Distance(g20,g3) = 3.8
    c: Distance(g21) = 9.5
    c: Coincident(g23,g24)
    c: Coincident(g24,g25)
    c: Coincident(g25,g26)
    c: Coincident(g26,g23)
    c: Horizontal(g24)
    c: Horizontal(g26)
    c: Vertical(g23)
    c: Vertical(g25)
    c: Symmetric(g24,g23,g27)
    c: PointOnObject(g27,g-2)
    c: Distance(g25) = 1.2
    c: Coincident(g28,g29)
    c: Coincident(g29,g30)
    c: Coincident(g30,g31)
    c: Coincident(g31,g28)
    c: Horizontal(g29)
    c: Horizontal(g31)
    c: Vertical(g28)
    c: Vertical(g30)
    c: Symmetric(g29,g28,g32)
    c: Distance(g30) = 13
    c: Distance(g29) = 13
    c: Distance(g30,g7) = 2
    c: Distance(g24,g7) = 2.3
    c: Distance(g32,g-2) = 15.6
    c: Coincident(g33,g34)
    c: Coincident(g34,g35)
    c: Coincident(g35,g36)
    c: Coincident(g36,g33)
    c: Horizontal(g34)
    c: Horizontal(g36)
    c: Vertical(g33)
    c: Vertical(g35)
    c: Symmetric(g34,g33,g37)
    c: Distance(g33) = 1.6
    c: Distance(g33,g5) = 0.6
    c: Coincident(g38,g39)
    c: Coincident(g39,g40)
    c: Coincident(g40,g41)
    c: Coincident(g41,g38)
    c: Horizontal(g39)
    c: Horizontal(g41)
    c: Vertical(g38)
    c: Vertical(g40)
    c: Symmetric(g39,g38,g42)
    c: PointOnObject(g39,g34)
    c: Distance(g40) = 6.4
    c: Coincident(g43,g37)
    c: Coincident(g43,g42)
    c: Vertical(g43)
    c: Coincident(g44,g45)
    c: Coincident(g45,g46)
    c: Coincident(g46,g47)
    c: Coincident(g47,g44)
    c: Horizontal(g45)
    c: Horizontal(g47)
    c: Vertical(g44)
    c: Vertical(g46)
    c: Symmetric(g45,g44,g48)
    c: PointOnObject(g48,g43)
    c: PointOnObject(g45,g5)
    c: Distance(g44) = 5.3
    c: Coincident(g49,g50)
    c: Coincident(g50,g51)
    c: Coincident(g51,g52)
    c: Coincident(g52,g49)
    c: Horizontal(g50)
    c: Horizontal(g52)
    c: Vertical(g49)
    c: Vertical(g51)
    c: Symmetric(g50,g49,g53)
    c: PointOnObject(g53,g43)
    c: Distance(g49,g47) = 4
    c: Diameter(g54) = 25
    c: Distance(g54,g24) = 12.8
    c: Distance(g33,g24) = 4.5
    c: Coincident(g55,g56)
    c: Coincident(g56,g57)
    c: Coincident(g57,g58)
    c: Coincident(g58,g55)
    c: Horizontal(g56)
    c: Horizontal(g58)
    c: Vertical(g55)
    c: Vertical(g57)
    c: Symmetric(g56,g55,g59)
    c: PointOnObject(g59,g-2)
    c: PointOnObject(g56,g16)
    c: Distance(g57) = 2.3
    c: Distance(g56) = 5.3
    c: Horizontal(g61)
    c: Horizontal(g63)
    c: Vertical(g60)
    c: Vertical(g62)
    c: Symmetric(g72,g68,g64)
    c: PointOnObject(g64,g-2)
    c: Distance(g72,g66) = 9.3
    c: Distance(g68,g66) = 3.3
    c: Distance(g68,g3) = 0.35
    c: PointOnObject(g66,g61)
    c: PointOnObject(g66,g60)
    c: Tangent(g61,g65) = 1.5708
    c: Tangent(g60,g65) = 1.5708
    c: PointOnObject(g68,g60)
    c: PointOnObject(g68,g63)
    c: Tangent(g60,g67) = 1.5708
    c: Tangent(g63,g67) = 1.5708
    c: PointOnObject(g70,g63)
    c: PointOnObject(g70,g62)
    c: Tangent(g63,g69) = 1.5708
    c: Tangent(g62,g69) = 1.5708
    c: PointOnObject(g72,g62)
    c: PointOnObject(g72,g61)
    c: Tangent(g62,g71) = 1.5708
    c: Tangent(g61,g71) = 1.5708
    c: Radius(g71) = 0.5
    c: Radius(g69) = 0.5
    c: Radius(g67) = 0.5
    c: Radius(g65) = 0.5
FEATURE [Sketcher::SketchObject] Sketch012
  ArcFitTolerance = 0
  AttachmentSupport = -> [XY_Plane]
  ExternalTypes = [0]
  FullyConstrained = true
  MakeInternals = false
  MapMode = 5
  _ExternalGeoVersion = 0
  sketch-geometry (7):
    g0: LineSegment StartX=1.1 StartY=-35.4 StartZ=0 EndX=0.55 EndY=-34.4474 EndZ=0
    g1: LineSegment StartX=0.55 StartY=-34.4474 StartZ=0 EndX=-0.55 EndY=-34.4474 EndZ=0
    g2: LineSegment StartX=-0.55 StartY=-34.4474 StartZ=0 EndX=-1.1 EndY=-35.4 EndZ=0
    g3: LineSegment StartX=-1.1 StartY=-35.4 StartZ=0 EndX=-0.55 EndY=-36.3526 EndZ=0
    g4: LineSegment StartX=-0.55 StartY=-36.3526 StartZ=0 EndX=0.55 EndY=-36.3526 EndZ=0
    g5: LineSegment StartX=0.55 StartY=-36.3526 StartZ=0 EndX=1.1 EndY=-35.4 EndZ=0
    g6: Circle [constr] CenterX=0 CenterY=-35.4 CenterZ=0 NormalX=0 NormalY=0 NormalZ=1 AngleXU=0 Radius=1.1
  constraints (17):
    c: Coincident(g0,g1)
    c: Coincident(g1,g2)
    c: Coincident(g2,g3)
    c: Coincident(g3,g4)
    c: Coincident(g4,g5)
    c: Coincident(g5,g0)
    c: Equal(g0, g1-g5) x5
    c: PointOnObject(g0,g6)
    c: PointOnObject(g1,g6)
    c: PointOnObject(g2,g6)
    c: PointOnObject(g3,g6)
    c: PointOnObject(g4,g6)
    c: PointOnObject(g5,g6)
    c: PointOnObject(g6,g-2)
    c: Diameter(g6) = 2.2
    c: Distance(g6,g-1) = 35.4
    c: Horizontal(g4)
FEATURE [Sketcher::SketchObject] Sketch013
  ArcFitTolerance = 0
  AttachmentSupport = -> [XY_Plane]
  ExternalTypes = [0]
  FullyConstrained = false
  MakeInternals = false
  MapMode = 5
  _ExternalGeoVersion = 0
  sketch-geometry (23):
    g0: ArcOfCircle [constr] CenterX=-17 CenterY=-63.1 CenterZ=0 NormalX=0 NormalY=0 NormalZ=1 AngleXU=0 Radius=1.25 StartAngle=3.14159 EndAngle=6.28319
    g1: ArcOfCircle [constr] CenterX=-17 CenterY=-62.3 CenterZ=0 NormalX=0 NormalY=0 NormalZ=1 AngleXU=0 Radius=1.25 StartAngle=8.7e-15 EndAngle=3.14159
    g2: LineSegment [constr] StartX=-15.75 StartY=-63.1 StartZ=0 EndX=-15.75 EndY=-62.3 EndZ=0
    g3: LineSegment StartX=-18.25 StartY=-62.3 StartZ=0 EndX=-18.25 EndY=-63.1 EndZ=0
    g4: LineSegment [constr] StartX=-17 StartY=-63.1 StartZ=0 EndX=-17 EndY=12.3674 EndZ=0
    g5: ArcOfCircle [constr] CenterX=-17 CenterY=-1.3 CenterZ=0 NormalX=0 NormalY=0 NormalZ=1 AngleXU=0 Radius=1.25 StartAngle=0 EndAngle=3.14159
    g6: ArcOfCircle [constr] CenterX=-17 CenterY=-2.1 CenterZ=0 NormalX=0 NormalY=0 NormalZ=1 AngleXU=0 Radius=1.25 StartAngle=3.14159 EndAngle=6.28319
    g7: LineSegment StartX=-18.25 StartY=-1.3 StartZ=0 EndX=-18.25 EndY=-2.1 EndZ=0
    g8: LineSegment [constr] StartX=-15.75 StartY=-2.1 StartZ=0 EndX=-15.75 EndY=-1.3 EndZ=0
    g9: LineSegment [constr] StartX=-15.75 StartY=-62.3 StartZ=0 EndX=-15.75 EndY=-2.1 EndZ=0
    g10: LineSegment StartX=-18.25 StartY=-2.1 StartZ=0 EndX=-18.25 EndY=-62.3 EndZ=0
    g11: ArcOfCircle CenterX=-17 CenterY=-1.3 CenterZ=0 NormalX=0 NormalY=0 NormalZ=1 AngleXU=0 Radius=1.25 StartAngle=1.5708 EndAngle=3.14159
    g12: ArcOfCircle CenterX=-17 CenterY=-63.1 CenterZ=0 NormalX=0 NormalY=0 NormalZ=1 AngleXU=0 Radius=1.25 StartAngle=3.14159 EndAngle=4.71239
    g13: LineSegment [constr] StartX=-17 StartY=-63.1 StartZ=0 EndX=-17 EndY=-64.35 EndZ=0
    g14: LineSegment StartX=-17 StartY=-0.05 StartZ=0 EndX=-14 EndY=-0.05 EndZ=0
    g15: LineSegment [constr] StartX=-18.25 StartY=-1.3 StartZ=0 EndX=-15.8528 EndY=-1.3 EndZ=0
    g16: LineSegment [constr] StartX=-14 StartY=-0.05 StartZ=0 EndX=-14 EndY=-64.5733 EndZ=0
    g17: LineSegment [constr] StartX=-17 StartY=-64.35 StartZ=0 EndX=-14 EndY=-64.35 EndZ=0
    g18: ArcOfCircle CenterX=-14 CenterY=-1.3 CenterZ=0 NormalX=0 NormalY=0 NormalZ=1 AngleXU=0 Radius=1.25 StartAngle=0 EndAngle=1.5708
    g19: LineSegment StartX=-12.75 StartY=-1.3 StartZ=0 EndX=-12.75 EndY=-63.1 EndZ=0
    g20: LineSegment [constr] StartX=-17 StartY=-63.1 StartZ=0 EndX=-12.75 EndY=-63.1 EndZ=0
    g21: ArcOfCircle CenterX=-14 CenterY=-63.1 CenterZ=0 NormalX=0 NormalY=0 NormalZ=1 AngleXU=0 Radius=1.25 StartAngle=4.71239 EndAngle=6.28319
    g22: LineSegment StartX=-14 StartY=-64.35 StartZ=0 EndX=-17 EndY=-64.35 EndZ=0
  constraints (59):
    c: Tangent(g0,g2) = -1.5708
    c: Tangent(g2,g1) = -1.5708
    c: Tangent(g1,g3) = -1.5708
    c: Tangent(g3,g0) = -1.5708
    c: Equal(g0,g1)
    c: Vertical(g2)
    c: Coincident(g4,g0)
    c: Vertical(g4)
    c: DistanceX(g-2,g0) = -17
    c: Distance(g1,g0) = 0.8
    c: Tangent(g5,g7) = -1.5708
    c: Tangent(g7,g6) = -1.5708
    c: Tangent(g6,g8) = -1.5708
    c: Tangent(g8,g5) = -1.5708
    c: Equal(g5,g6)
    c: PointOnObject(g5,g4)
    c: PointOnObject(g6,g4)
    c: Distance(g5,g8) = 2.5
    c: Distance(g5,g6) = 0.8
    c: Distance(g5,g-1) = 1.3
    c: Distance(g5,g1) = 61
    c: Coincident(g9,g2)
    c: Coincident(g9,g8)
    c: Vertical(g9)
    c: Coincident(g10,g7)
    c: Coincident(g10,g3)
    c: Coincident(g11,g5)
    c: Coincident(g11,g7)
    c: PointOnObject(g11,g4)
    c: Coincident(g12,g0)
    c: Coincident(g12,g3)
    c: Coincident(g13,g12)
    c: Coincident(g13,g12)
    c: Vertical(g13)
    c: Coincident(g14,g11)
    c: Horizontal(g14)
    c: Coincident(g15,g7)
    c: Horizontal(g15)
    c: Coincident(g16,g14)
    c: Vertical(g16)
    c: Coincident(g17,g12)
    c: PointOnObject(g17,g16)
    c: Horizontal(g17)
    c: PointOnObject(g18,g15)
    c: Coincident(g18,g14)
    c: PointOnObject(g18,g15)
    c: PointOnObject(g18,g16)
    c: Coincident(g19,g18)
    c: Vertical(g19)
    c: Coincident(g20,g12)
    c: Coincident(g20,g19)
    c: Horizontal(g20)
    c: PointOnObject(g21,g20)
    c: Coincident(g21,g19)
    c: PointOnObject(g21,g16)
    c: PointOnObject(g21,g16)
    c: Coincident(g22,g21)
    c: Coincident(g22,g12)
    c: Distance(g14) = 3
FEATURE [Sketcher::SketchObject] Sketch014
  ArcFitTolerance = 0
  AttachmentOffset = pos=(0,0,4.5) rot=(0,0,1;0rad)
  AttachmentSupport = -> [XY_Plane]
  ExternalTypes = [0]
  FullyConstrained = true
  MakeInternals = false
  MapMode = 5
  Placement = pos=(0,0,4.5) rot=(0,0,1;0rad)
  _ExternalGeoVersion = 0
  expr: Constraints[10] = Sketch001.Constraints[10]
  expr: Constraints[12] = Sketch001.Constraints[12]
  expr: Constraints[22] = Sketch001.Constraints[22]
  expr: Constraints[23] = Sketch001.Constraints[23]
  expr: Constraints[24] = Sketch001.Constraints[24]
  expr: Constraints[36] = Sketch001.Constraints[36]
  expr: Constraints[37] = Sketch001.Constraints[37]
  expr: Constraints[48] = Sketch001.Constraints[48]
  expr: Constraints[49] = Sketch001.Constraints[49]
  expr: Constraints[50] = Sketch001.Constraints[50]
  expr: Constraints[51] = Sketch001.Constraints[51]
  sketch-geometry (25):
    g0: LineSegment [constr] StartX=8.4 StartY=-34 StartZ=0 EndX=8.4 EndY=0 EndZ=0
    g1: LineSegment [constr] StartX=8.4 StartY=0 StartZ=0 EndX=-8.4 EndY=0 EndZ=0
    g2: LineSegment [constr] StartX=-8.4 StartY=0 StartZ=0 EndX=-8.4 EndY=-34 EndZ=0
    g3: LineSegment [constr] StartX=-8.4 StartY=-34 StartZ=0 EndX=8.4 EndY=-34 EndZ=0
    g4: GeomPoint [constr] X=0 Y=-17 Z=0
    g5: LineSegment [constr] StartX=-22.1 StartY=-60.7 StartZ=0 EndX=-22.1 EndY=-3.7 EndZ=0
    g6: LineSegment [constr] StartX=-22.1 StartY=-3.7 StartZ=0 EndX=-9.1 EndY=-3.7 EndZ=0
    g7: LineSegment [constr] StartX=-9.1 StartY=-3.7 StartZ=0 EndX=-9.1 EndY=-60.7 EndZ=0
    g8: LineSegment [constr] StartX=-9.1 StartY=-60.7 StartZ=0 EndX=-22.1 EndY=-60.7 EndZ=0
    g9: GeomPoint [constr] X=-15.6 Y=-32.2 Z=0
    g10: LineSegment [constr] StartX=22.1 StartY=-68.9 StartZ=0 EndX=22.1 EndY=0 EndZ=0
    g11: LineSegment [constr] StartX=22.1 StartY=0 StartZ=0 EndX=-22.1 EndY=0 EndZ=0
    g12: LineSegment [constr] StartX=-22.1 StartY=0 StartZ=0 EndX=-22.1 EndY=-68.9 EndZ=0
    g13: LineSegment [constr] StartX=-22.1 StartY=-68.9 StartZ=0 EndX=22.1 EndY=-68.9 EndZ=0
    g14: GeomPoint [constr] X=0 Y=-34.45 Z=0
    g15: LineSegment [constr] StartX=8.5 StartY=-53.9 StartZ=0 EndX=8.5 EndY=-36.9 EndZ=0
    g16: LineSegment [constr] StartX=8.5 StartY=-36.9 StartZ=0 EndX=-8.5 EndY=-36.9 EndZ=0
    g17: LineSegment [constr] StartX=-8.5 StartY=-36.9 StartZ=0 EndX=-8.5 EndY=-53.9 EndZ=0
    g18: LineSegment [constr] StartX=-8.5 StartY=-53.9 StartZ=0 EndX=8.5 EndY=-53.9 EndZ=0
    g19: GeomPoint [constr] X=0 Y=-45.4 Z=0
    g20: LineSegment StartX=-8.5 StartY=-36.6 StartZ=0 EndX=-8.5 EndY=-34.5 EndZ=0
    g21: LineSegment StartX=-8.5 StartY=-34.5 StartZ=0 EndX=8.5 EndY=-34.5 EndZ=0
    g22: LineSegment StartX=8.5 StartY=-34.5 StartZ=0 EndX=8.5 EndY=-36.6 EndZ=0
    g23: LineSegment StartX=8.5 StartY=-36.6 StartZ=0 EndX=-8.5 EndY=-36.6 EndZ=0
    g24: GeomPoint [constr] X=0 Y=-35.55 Z=0
  constraints (65):
    c: Coincident(g0,g1)
    c: Coincident(g1,g2)
    c: Coincident(g2,g3)
    c: Coincident(g3,g0)
    c: Horizontal(g1)
    c: Horizontal(g3)
    c: Vertical(g0)
    c: Vertical(g2)
    c: Symmetric(g1,g0,g4)
    c: PointOnObject(g4,g-2)
    c: Distance(g0) = 34
    c: PointOnObject(g-1,g1)
    c: Distance(g3) = 16.8
    c: Coincident(g5,g6)
    c: Coincident(g6,g7)
    c: Coincident(g7,g8)
    c: Coincident(g8,g5)
    c: Horizontal(g6)
    c: Horizontal(g8)
    c: Vertical(g5)
    c: Vertical(g7)
    c: Symmetric(g6,g5,g9)
    c: Distance(g6) = 13
    c: Distance(g5) = 57
    c: Distance(g9,g-1) = 32.2
    c: Coincident(g10,g11)
    c: Coincident(g11,g12)
    c: Coincident(g12,g13)
    c: Coincident(g13,g10)
    c: Horizontal(g11)
    c: Horizontal(g13)
    c: Vertical(g10)
    c: Vertical(g12)
    c: Symmetric(g11,g10,g14)
    c: PointOnObject(g14,g-2)
    c: PointOnObject(g11,g-1)
    c: Distance(g12,g-2) = 22.1
    c: Distance(g10) = 68.9
    c: Coincident(g15,g16)
    c: Coincident(g16,g17)
    c: Coincident(g17,g18)
    c: Coincident(g18,g15)
    c: Horizontal(g16)
    c: Horizontal(g18)
    c: Vertical(g15)
    c: Vertical(g17)
    c: Symmetric(g16,g15,g19)
    c: PointOnObject(g19,g-2)
    c: Distance(g18) = 17
    c: Distance(g15) = 17
    c: Distance(g19,g-1) = 45.4
    c: Distance(g9,g-2) = 15.6
    c: Coincident(g20,g21)
    c: Coincident(g21,g22)
    c: Coincident(g22,g23)
    c: Coincident(g23,g20)
    c: Horizontal(g21)
    c: Horizontal(g23)
    c: Vertical(g20)
    c: Vertical(g22)
    c: Symmetric(g21,g20,g24)
    c: PointOnObject(g24,g-2)
    c: Distance(g22) = 2.1
    c: Distance(g21) = 17
    c: Distance(g16,g23) = 0.3
FEATURE [Sketcher::SketchObject] Sketch016
  ArcFitTolerance = 0
  AttachmentSupport = -> [XZ_Plane]
  ExternalTypes = [0]
  FullyConstrained = false
  MakeInternals = false
  MapMode = 5
  Placement = pos=(0,0,0) rot=(1,0,0;1.5708rad)
  _ExternalGeoVersion = 0
  expr: Constraints[105] = Sketch.Constraints[105]
  expr: Constraints[120] = Sketch.Constraints[120]
  expr: Constraints[131] = Sketch.Constraints[131]
  expr: Constraints[132] = Sketch.Constraints[132]
  expr: Constraints[133] = Sketch.Constraints[133]
  expr: Constraints[19] = Sketch.Constraints[19]
  expr: Constraints[20] = Sketch.Constraints[20]
  expr: Constraints[31] = Sketch.Constraints[31]
  expr: Constraints[32] = Sketch.Constraints[32]
  expr: Constraints[44] = Sketch.Constraints[44]
  expr: Constraints[45] = Sketch.Constraints[45]
  expr: Constraints[57] = Sketch.Constraints[57]
  expr: Constraints[58] = Sketch.Constraints[58]
  expr: Constraints[69] = Sketch.Constraints[69]
  expr: Constraints[79] = Sketch.Constraints[79]
  expr: Constraints[80] = Sketch.Constraints[80]
  expr: Constraints[81] = Sketch.Constraints[81]
  expr: Constraints[82] = Sketch.Constraints[82]
  expr: Constraints[83] = Sketch.Constraints[83]
  expr: Constraints[93] = Sketch.Constraints[93]
  expr: Constraints[94] = Sketch.Constraints[94]
  sketch-geometry (62):
    g0: LineSegment [constr] StartX=9 StartY=2.5 StartZ=0 EndX=9 EndY=4.1 EndZ=0
    g1: LineSegment [constr] StartX=9 StartY=4.1 StartZ=0 EndX=-9 EndY=4.1 EndZ=0
    g2: LineSegment [constr] StartX=-9 StartY=4.1 StartZ=0 EndX=-9 EndY=2.5 EndZ=0
    g3: LineSegment [constr] StartX=-9 StartY=2.5 StartZ=0 EndX=9 EndY=2.5 EndZ=0
    g4: GeomPoint [constr] X=0 Y=3.3 Z=0
    g5: LineSegment [constr] StartX=-105.409 StartY=0 StartZ=0 EndX=45.7381 EndY=0 EndZ=0
    g6: LineSegment [constr] StartX=45.7381 StartY=0 StartZ=0 EndX=45.7381 EndY=-1.6 EndZ=0
    g7: LineSegment [constr] StartX=45.7381 StartY=-1.6 StartZ=0 EndX=-105.409 EndY=-1.6 EndZ=0
    g8: LineSegment [constr] StartX=-105.409 StartY=-1.6 StartZ=0 EndX=-105.409 EndY=0 EndZ=0
    g9: LineSegment [constr] StartX=9 StartY=2.5 StartZ=0 EndX=6.36312 EndY=2.5 EndZ=0
    g10: LineSegment [constr] StartX=6.36312 StartY=2.5 StartZ=0 EndX=6.36312 EndY=0 EndZ=0
    g11: LineSegment [constr] StartX=6.36312 StartY=0 StartZ=0 EndX=9 EndY=0 EndZ=0
    g12: LineSegment [constr] StartX=9 StartY=0 StartZ=0 EndX=9 EndY=2.5 EndZ=0
    g13: LineSegment [constr] StartX=4.55 StartY=-5.1 StartZ=0 EndX=4.55 EndY=-1.6 EndZ=0
    g14: LineSegment [constr] StartX=4.55 StartY=-1.6 StartZ=0 EndX=-4.55 EndY=-1.6 EndZ=0
    g15: LineSegment [constr] StartX=-4.55 StartY=-1.6 StartZ=0 EndX=-4.55 EndY=-5.1 EndZ=0
    g16: LineSegment [constr] StartX=-4.55 StartY=-5.1 StartZ=0 EndX=4.55 EndY=-5.1 EndZ=0
    g17: GeomPoint [constr] X=0 Y=-3.35 Z=0
    g18: LineSegment [constr] StartX=-4.75 StartY=6.3 StartZ=0 EndX=-4.75 EndY=4.1 EndZ=0
    g19: LineSegment [constr] StartX=-4.75 StartY=4.1 StartZ=0 EndX=4.75 EndY=4.1 EndZ=0
    g20: LineSegment [constr] StartX=4.75 StartY=4.1 StartZ=0 EndX=4.75 EndY=6.3 EndZ=0
    g21: LineSegment [constr] StartX=4.75 StartY=6.3 StartZ=0 EndX=-4.75 EndY=6.3 EndZ=0
    g22: GeomPoint [constr] X=0 Y=5.2 Z=0
    g23: LineSegment [constr] StartX=-44.4822 StartY=-5.1 StartZ=0 EndX=-44.4822 EndY=-3.9 EndZ=0
    g24: LineSegment [constr] StartX=-44.4822 StartY=-3.9 StartZ=0 EndX=44.4822 EndY=-3.9 EndZ=0
    g25: LineSegment [constr] StartX=44.4822 StartY=-3.9 StartZ=0 EndX=44.4822 EndY=-5.1 EndZ=0
    g26: LineSegment [constr] StartX=44.4822 StartY=-5.1 StartZ=0 EndX=-44.4822 EndY=-5.1 EndZ=0
    g27: GeomPoint [constr] X=0 Y=-4.5 Z=0
    g28: LineSegment [constr] StartX=-9.1 StartY=-3.6 StartZ=0 EndX=-9.1 EndY=9.4 EndZ=0
    g29: LineSegment [constr] StartX=-9.1 StartY=9.4 StartZ=0 EndX=-22.1 EndY=9.4 EndZ=0
    g30: LineSegment [constr] StartX=-22.1 StartY=9.4 StartZ=0 EndX=-22.1 EndY=-3.6 EndZ=0
    g31: LineSegment [constr] StartX=-22.1 StartY=-3.6 StartZ=0 EndX=-9.1 EndY=-3.6 EndZ=0
    g32: GeomPoint [constr] X=-15.6 Y=2.9 Z=0
    g33: LineSegment [constr] StartX=33.0788 StartY=0.6 StartZ=0 EndX=33.0788 EndY=2.2 EndZ=0
    g34: LineSegment [constr] StartX=33.0788 StartY=2.2 StartZ=0 EndX=11.9844 EndY=2.2 EndZ=0
    g35: LineSegment [constr] StartX=11.9844 StartY=2.2 StartZ=0 EndX=11.9844 EndY=0.6 EndZ=0
    g36: LineSegment [constr] StartX=11.9844 StartY=0.6 StartZ=0 EndX=33.0788 EndY=0.6 EndZ=0
    g37: GeomPoint [constr] X=22.5316 Y=1.4 Z=0
    g38: LineSegment [constr] StartX=25.7428 StartY=8.6 StartZ=0 EndX=25.7428 EndY=2.2 EndZ=0
    g39: LineSegment [constr] StartX=25.7428 StartY=2.2 StartZ=0 EndX=19.3204 EndY=2.2 EndZ=0
    g40: LineSegment [constr] StartX=19.3204 StartY=2.2 StartZ=0 EndX=19.3204 EndY=8.6 EndZ=0
    g41: LineSegment [constr] StartX=19.3204 StartY=8.6 StartZ=0 EndX=25.7428 EndY=8.6 EndZ=0
    g42: GeomPoint [constr] X=22.5316 Y=5.4 Z=0
    g43: LineSegment [constr] StartX=22.5316 StartY=1.4 StartZ=0 EndX=22.5316 EndY=5.4 EndZ=0
    g44: LineSegment [constr] StartX=29.8817 StartY=5.3 StartZ=0 EndX=29.8817 EndY=0 EndZ=0
    g45: LineSegment [constr] StartX=29.8817 StartY=0 StartZ=0 EndX=15.1815 EndY=0 EndZ=0
    g46: LineSegment [constr] StartX=15.1815 StartY=0 StartZ=0 EndX=15.1815 EndY=5.3 EndZ=0
    g47: LineSegment [constr] StartX=15.1815 StartY=5.3 StartZ=0 EndX=29.8817 EndY=5.3 EndZ=0
    g48: GeomPoint [constr] X=22.5316 Y=2.65 Z=0
    g49: LineSegment [constr] StartX=28.1684 StartY=6.59315 StartZ=0 EndX=28.1684 EndY=9.3 EndZ=0
    g50: LineSegment [constr] StartX=28.1684 StartY=9.3 StartZ=0 EndX=16.8947 EndY=9.3 EndZ=0
    g51: LineSegment [constr] StartX=16.8947 StartY=9.3 StartZ=0 EndX=16.8947 EndY=6.59315 EndZ=0
    g52: LineSegment [constr] StartX=16.8947 StartY=6.59315 StartZ=0 EndX=28.1684 EndY=6.59315 EndZ=0
    g53: GeomPoint [constr] X=22.5316 Y=7.94657 Z=0
    g54: Circle [constr] CenterX=41.3382 CenterY=8.9 CenterZ=0 NormalX=0 NormalY=0 NormalZ=1 AngleXU=0 Radius=12.5
    g55: LineSegment [constr] StartX=-18.7 StartY=4.8 StartZ=0 EndX=-18.7 EndY=10.6 EndZ=0
    g56: LineSegment [constr] StartX=-18.7 StartY=4.8 StartZ=0 EndX=-30.5234 EndY=4.8 EndZ=0
    g57: ArcOfCircle CenterX=-18.7 CenterY=4.8 CenterZ=0 NormalX=0 NormalY=0 NormalZ=1 AngleXU=0 Radius=5.8 StartAngle=1.5708 EndAngle=3.14159
    g58: LineSegment StartX=-24.5 StartY=4.8 StartZ=0 EndX=-32.4732 EndY=4.8 EndZ=0
    g59: LineSegment StartX=-32.4732 StartY=4.8 StartZ=0 EndX=-32.4732 EndY=15.4079 EndZ=0
    g60: LineSegment StartX=-32.4732 StartY=15.4079 StartZ=0 EndX=-18.7 EndY=15.4079 EndZ=0
    g61: LineSegment StartX=-18.7 StartY=15.4079 StartZ=0 EndX=-18.7 EndY=10.6 EndZ=0
  constraints (153):
    c: Coincident(g0,g1)
    c: Coincident(g1,g2)
    c: Coincident(g2,g3)
    c: Coincident(g3,g0)
    c: Horizontal(g1)
    c: Horizontal(g3)
    c: Vertical(g0)
    c: Vertical(g2)
    c: Symmetric(g1,g0,g4)
    c: PointOnObject(g4,g-2)
    c: Coincident(g5,g6)
    c: Coincident(g6,g7)
    c: Coincident(g7,g8)
    c: Coincident(g8,g5)
    c: Horizontal(g5)
    c: Horizontal(g7)
    c: Vertical(g6)
    c: Vertical(g8)
    c: PointOnObject(g5,g-1)
    c: Distance(g6) = 1.6
    c: Distance(g0) = 1.6
    c: Coincident(g9,g10)
    c: Coincident(g10,g11)
    c: Coincident(g11,g12)
    c: Coincident(g12,g9)
    c: Horizontal(g9)
    c: Horizontal(g11)
    c: Vertical(g10)
    c: Vertical(g12)
    c: Coincident(g9,g0)
    c: PointOnObject(g10,g5)
    c: Distance(g12) = 2.5
    c: Distance(g1) = 18
    c: Coincident(g13,g14)
    c: Coincident(g14,g15)
    c: Coincident(g15,g16)
    c: Coincident(g16,g13)
    c: Horizontal(g14)
    c: Horizontal(g16)
    c: Vertical(g13)
    c: Vertical(g15)
    c: Symmetric(g14,g13,g17)
    c: PointOnObject(g17,g-2)
    c: PointOnObject(g14,g7)
    c: Distance(g13) = 3.5
    c: Distance(g16) = 9.1
    c: Coincident(g18,g19)
    c: Coincident(g19,g20)
    c: Coincident(g20,g21)
    c: Coincident(g21,g18)
    c: Horizontal(g19)
    c: Horizontal(g21)
    c: Vertical(g18)
    c: Vertical(g20)
    c: Symmetric(g19,g18,g22)
    c: PointOnObject(g22,g-2)
    c: PointOnObject(g19,g1)
    c: Distance(g20,g3) = 3.8
    c: Distance(g21) = 9.5
    c: Coincident(g23,g24)
    c: Coincident(g24,g25)
    c: Coincident(g25,g26)
    c: Coincident(g26,g23)
    c: Horizontal(g24)
    c: Horizontal(g26)
    c: Vertical(g23)
    c: Vertical(g25)
    c: Symmetric(g24,g23,g27)
    c: PointOnObject(g27,g-2)
    c: Distance(g25) = 1.2
    c: Coincident(g28,g29)
    c: Coincident(g29,g30)
    c: Coincident(g30,g31)
    c: Coincident(g31,g28)
    c: Horizontal(g29)
    c: Horizontal(g31)
    c: Vertical(g28)
    c: Vertical(g30)
    c: Symmetric(g29,g28,g32)
    c: Distance(g30) = 13
    c: Distance(g29) = 13
    c: Distance(g30,g7) = 2
    c: Distance(g24,g7) = 2.3
    c: Distance(g32,g-2) = 15.6
    c: Coincident(g33,g34)
    c: Coincident(g34,g35)
    c: Coincident(g35,g36)
    c: Coincident(g36,g33)
    c: Horizontal(g34)
    c: Horizontal(g36)
    c: Vertical(g33)
    c: Vertical(g35)
    c: Symmetric(g34,g33,g37)
    c: Distance(g33) = 1.6
    c: Distance(g33,g5) = 0.6
    c: Coincident(g38,g39)
    c: Coincident(g39,g40)
    c: Coincident(g40,g41)
    c: Coincident(g41,g38)
    c: Horizontal(g39)
    c: Horizontal(g41)
    c: Vertical(g38)
    c: Vertical(g40)
    c: Symmetric(g39,g38,g42)
    c: PointOnObject(g39,g34)
    c: Distance(g40) = 6.4
    c: Coincident(g43,g37)
    c: Coincident(g43,g42)
    c: Vertical(g43)
    c: Coincident(g44,g45)
    c: Coincident(g45,g46)
    c: Coincident(g46,g47)
    c: Coincident(g47,g44)
    c: Horizontal(g45)
    c: Horizontal(g47)
    c: Vertical(g44)
    c: Vertical(g46)
    c: Symmetric(g45,g44,g48)
    c: PointOnObject(g48,g43)
    c: PointOnObject(g45,g5)
    c: Distance(g44) = 5.3
    c: Coincident(g49,g50)
    c: Coincident(g50,g51)
    c: Coincident(g51,g52)
    c: Coincident(g52,g49)
    c: Horizontal(g50)
    c: Horizontal(g52)
    c: Vertical(g49)
    c: Vertical(g51)
    c: Symmetric(g50,g49,g53)
    c: PointOnObject(g53,g43)
    c: Distance(g49,g47) = 4
    c: Diameter(g54) = 25
    c: Distance(g54,g24) = 12.8
    c: Distance(g33,g24) = 4.5
    c: Vertical(g55)
    c: Coincident(g56,g55)
    c: Horizontal(g56)
    c: Coincident(g57,g55)
    c: Coincident(g57,g55)
    c: PointOnObject(g57,g56)
    c: Distance(g57,g29) = 1.2
    c: Coincident(g58,g57)
    c: Horizontal(g58)
    c: Coincident(g59,g58)
    c: Vertical(g59)
    c: Coincident(g60,g59)
    c: Horizontal(g60)
    c: Coincident(g61,g60)
    c: Coincident(g61,g57)
    c: Vertical(g61)
    c: DistanceX(g57,g-1) = 24.5
    c: Radius(g57) = 5.8
FEATURE [Sketcher::SketchObject] Sketch017
  ArcFitTolerance = 0
  AttachmentOffset = pos=(0,0,-1.6) rot=(0,0,1;0rad)
  AttachmentSupport = -> [XY_Plane]
  ExternalTypes = [0]
  FullyConstrained = false
  MakeInternals = false
  MapMode = 5
  Placement = pos=(0,0,-1.6) rot=(0,0,1;0rad)
  _ExternalGeoVersion = 0
  expr: .AttachmentOffset.Base.z = -1.6
  expr: Constraints[10] = Sketch001.Constraints[10]
  expr: Constraints[12] = Sketch001.Constraints[12]
  expr: Constraints[22] = Sketch001.Constraints[22]
  expr: Constraints[23] = Sketch001.Constraints[23]
  expr: Constraints[24] = Sketch001.Constraints[24]
  expr: Constraints[31] = Sketch001.Constraints[37]
  expr: Constraints[42] = Sketch001.Constraints[48]
  expr: Constraints[43] = Sketch001.Constraints[49]
  expr: Constraints[44] = Sketch001.Constraints[50]
  expr: Constraints[45] = Sketch001.Constraints[51]
  sketch-geometry (30):
    g0: LineSegment [constr] StartX=8.4 StartY=-34 StartZ=0 EndX=8.4 EndY=0 EndZ=0
    g1: LineSegment [constr] StartX=8.4 StartY=0 StartZ=0 EndX=-8.4 EndY=0 EndZ=0
    g2: LineSegment [constr] StartX=-8.4 StartY=0 StartZ=0 EndX=-8.4 EndY=-34 EndZ=0
    g3: LineSegment [constr] StartX=-8.4 StartY=-34 StartZ=0 EndX=8.4 EndY=-34 EndZ=0
    g4: GeomPoint [constr] X=0 Y=-17 Z=0
    g5: LineSegment [constr] StartX=-22.1 StartY=-60.7 StartZ=0 EndX=-22.1 EndY=-3.7 EndZ=0
    g6: LineSegment [constr] StartX=-22.1 StartY=-3.7 StartZ=0 EndX=-9.1 EndY=-3.7 EndZ=0
    g7: LineSegment [constr] StartX=-9.1 StartY=-3.7 StartZ=0 EndX=-9.1 EndY=-60.7 EndZ=0
    g8: LineSegment [constr] StartX=-9.1 StartY=-60.7 StartZ=0 EndX=-22.1 EndY=-60.7 EndZ=0
    g9: GeomPoint [constr] X=-15.6 Y=-32.2 Z=0
    g10: LineSegment [constr] StartX=21.5 StartY=-68.9 StartZ=0 EndX=21.5 EndY=0 EndZ=0
    g11: LineSegment [constr] StartX=21.5 StartY=0 StartZ=0 EndX=-21.5 EndY=0 EndZ=0
    g12: GeomPoint [constr] X=0 Y=-34.45 Z=0
    g13: LineSegment [constr] StartX=8.5 StartY=-53.9 StartZ=0 EndX=8.5 EndY=-36.9 EndZ=0
    g14: LineSegment [constr] StartX=8.5 StartY=-36.9 StartZ=0 EndX=-8.5 EndY=-36.9 EndZ=0
    g15: LineSegment [constr] StartX=-8.5 StartY=-36.9 StartZ=0 EndX=-8.5 EndY=-53.9 EndZ=0
    g16: LineSegment [constr] StartX=-8.5 StartY=-53.9 StartZ=0 EndX=8.5 EndY=-53.9 EndZ=0
    g17: GeomPoint [constr] X=0 Y=-45.4 Z=0
    g18: LineSegment StartX=-18.1 StartY=-59.7 StartZ=0 EndX=-24.1 EndY=-59.7 EndZ=0
    g19: LineSegment [constr] StartX=-24.1 StartY=-59.7 StartZ=0 EndX=-24.1 EndY=-64.7 EndZ=0
    g20: LineSegment [constr] StartX=-24.1 StartY=-64.7 StartZ=0 EndX=-18.1 EndY=-64.7 EndZ=0
    g21: LineSegment StartX=-18.1 StartY=-64.7 StartZ=0 EndX=-18.1 EndY=-59.7 EndZ=0
    g22: LineSegment [constr] StartX=-24.1 StartY=-3.3 StartZ=0 EndX=-24.1 EndY=-59.7 EndZ=0
    g23: LineSegment [constr] StartX=-18.1 StartY=-3.3 StartZ=0 EndX=-18.1 EndY=-59.7 EndZ=0
    g24: LineSegment StartX=-24.1 StartY=-59.7 StartZ=0 EndX=-22.2801 EndY=-64.7 EndZ=0
    g25: LineSegment StartX=-18.1 StartY=-64.7 StartZ=0 EndX=-22.2801 EndY=-64.7 EndZ=0
    g26: LineSegment StartX=5 StartY=0 StartZ=0 EndX=5 EndY=-1.2 EndZ=0
    g27: LineSegment StartX=5 StartY=-1.2 StartZ=0 EndX=9 EndY=-1.2 EndZ=0
    g28: LineSegment StartX=9 StartY=-1.2 StartZ=0 EndX=9 EndY=0 EndZ=0
    g29: LineSegment StartX=9 StartY=0 StartZ=0 EndX=5 EndY=0 EndZ=0
  constraints (79):
    c: Coincident(g0,g1)
    c: Coincident(g1,g2)
    c: Coincident(g2,g3)
    c: Coincident(g3,g0)
    c: Horizontal(g1)
    c: Horizontal(g3)
    c: Vertical(g0)
    c: Vertical(g2)
    c: Symmetric(g1,g0,g4)
    c: PointOnObject(g4,g-2)
    c: Distance(g0) = 34
    c: PointOnObject(g-1,g1)
    c: Distance(g3) = 16.8
    c: Coincident(g5,g6)
    c: Coincident(g6,g7)
    c: Coincident(g7,g8)
    c: Coincident(g8,g5)
    c: Horizontal(g6)
    c: Horizontal(g8)
    c: Vertical(g5)
    c: Vertical(g7)
    c: Symmetric(g6,g5,g9)
    c: Distance(g6) = 13
    c: Distance(g5) = 57
    c: Distance(g9,g-1) = 32.2
    c: Coincident(g10,g11)
    c: Horizontal(g11)
    c: Vertical(g10)
    c: Symmetric(g11,g10,g12)
    c: PointOnObject(g12,g-2)
    c: PointOnObject(g11,g-1)
    c: Distance(g10) = 68.9
    c: Coincident(g13,g14)
    c: Coincident(g14,g15)
    c: Coincident(g15,g16)
    c: Coincident(g16,g13)
    c: Horizontal(g14)
    c: Horizontal(g16)
    c: Vertical(g13)
    c: Vertical(g15)
    c: Symmetric(g14,g13,g17)
    c: PointOnObject(g17,g-2)
    c: Distance(g16) = 17
    c: Distance(g13) = 17
    c: Distance(g17,g-1) = 45.4
    c: Distance(g9,g-2) = 15.6
    c: Coincident(g18,g19)
    c: Coincident(g19,g20)
    c: Coincident(g20,g21)
    c: Coincident(g21,g18)
    c: Horizontal(g18)
    c: Horizontal(g20)
    c: Vertical(g19)
    c: Vertical(g21)
    c: Distance(g18,g8) = 1
    c: Distance(g19) = 5
    c: Distance(g20) = 6
    c: Distance(g20,g-2) = 18.1
    c: Coincident(g22,g18)
    c: Vertical(g22)
    c: Coincident(g23,g18)
    c: Vertical(g23)
    c: Coincident(g24,g18)
    c: PointOnObject(g24,g20)
    c: Coincident(g25,g20)
    c: Coincident(g25,g24)
    c: Coincident(g26,g27)
    c: Coincident(g27,g28)
    c: Coincident(g28,g29)
    c: Coincident(g29,g26)
    c: Vertical(g26)
    c: Vertical(g28)
    c: Horizontal(g27)
    c: Horizontal(g29)
    c: PointOnObject(g26,g1)
    c: DistanceX(g27,g27) = 4
    c: DistanceY(g28,g28) = 1.2
    c: DistanceX(g-1,g26) = 5
    c: Angle(g25,g24) = 1.91986
FEATURE [Sketcher::SketchObject] Sketch018
  ArcFitTolerance = 1e-06
  AttachmentSupport = -> [XY_Plane]
  ExternalTypes = [0]
  FullyConstrained = false
  MakeInternals = false
  MapMode = 5
  _ExternalGeoVersion = 0
  expr: Constraints[10] = Sketch001.Constraints[10]
  expr: Constraints[12] = Sketch001.Constraints[12]
  expr: Constraints[22] = Sketch001.Constraints[22]
  expr: Constraints[23] = Sketch001.Constraints[23]
  expr: Constraints[24] = Sketch001.Constraints[24]
  expr: Constraints[36] = Sketch001.Constraints[36]
  expr: Constraints[37] = Sketch001.Constraints[37]
  expr: Constraints[48] = Sketch001.Constraints[48]
  expr: Constraints[49] = Sketch001.Constraints[49]
  expr: Constraints[50] = Sketch001.Constraints[50]
  expr: Constraints[51] = Sketch001.Constraints[51]
  sketch-geometry (24):
    g0: LineSegment [constr] StartX=8.4 StartY=-34 StartZ=0 EndX=8.4 EndY=0 EndZ=0
    g1: LineSegment [constr] StartX=8.4 StartY=0 StartZ=0 EndX=-8.4 EndY=0 EndZ=0
    g2: LineSegment [constr] StartX=-8.4 StartY=0 StartZ=0 EndX=-8.4 EndY=-34 EndZ=0
    g3: LineSegment [constr] StartX=-8.4 StartY=-34 StartZ=0 EndX=8.4 EndY=-34 EndZ=0
    g4: GeomPoint [constr] X=0 Y=-17 Z=0
    g5: LineSegment [constr] StartX=-22.1 StartY=-60.7 StartZ=0 EndX=-22.1 EndY=-3.7 EndZ=0
    g6: LineSegment [constr] StartX=-22.1 StartY=-3.7 StartZ=0 EndX=-9.1 EndY=-3.7 EndZ=0
    g7: LineSegment [constr] StartX=-9.1 StartY=-3.7 StartZ=0 EndX=-9.1 EndY=-60.7 EndZ=0
    g8: LineSegment [constr] StartX=-9.1 StartY=-60.7 StartZ=0 EndX=-22.1 EndY=-60.7 EndZ=0
    g9: GeomPoint [constr] X=-15.6 Y=-32.2 Z=0
    g10: LineSegment [constr] StartX=22.1 StartY=-68.9 StartZ=0 EndX=22.1 EndY=0 EndZ=0
    g11: LineSegment [constr] StartX=22.1 StartY=0 StartZ=0 EndX=-22.1 EndY=0 EndZ=0
    g12: LineSegment [constr] StartX=-22.1 StartY=0 StartZ=0 EndX=-22.1 EndY=-68.9 EndZ=0
    g13: LineSegment [constr] StartX=-22.1 StartY=-68.9 StartZ=0 EndX=22.1 EndY=-68.9 EndZ=0
    g14: GeomPoint [constr] X=0 Y=-34.45 Z=0
    g15: LineSegment [constr] StartX=8.5 StartY=-53.9 StartZ=0 EndX=8.5 EndY=-36.9 EndZ=0
    g16: LineSegment [constr] StartX=8.5 StartY=-36.9 StartZ=0 EndX=-8.5 EndY=-36.9 EndZ=0
    g17: LineSegment [constr] StartX=-8.5 StartY=-36.9 StartZ=0 EndX=-8.5 EndY=-53.9 EndZ=0
    g18: LineSegment [constr] StartX=-8.5 StartY=-53.9 StartZ=0 EndX=8.5 EndY=-53.9 EndZ=0
    g19: GeomPoint [constr] X=0 Y=-45.4 Z=0
    g20: LineSegment StartX=-8.7 StartY=0 StartZ=0 EndX=-8.7 EndY=-40.9123 EndZ=0
    g21: LineSegment StartX=-8.7 StartY=-40.9123 StartZ=0 EndX=22.1 EndY=-40.9123 EndZ=0
    g22: LineSegment StartX=22.1 StartY=-40.9123 StartZ=0 EndX=22.1 EndY=0 EndZ=0
    g23: LineSegment StartX=22.1 StartY=0 StartZ=0 EndX=-8.7 EndY=0 EndZ=0
  constraints (63):
    c: Coincident(g0,g1)
    c: Coincident(g1,g2)
    c: Coincident(g2,g3)
    c: Coincident(g3,g0)
    c: Horizontal(g1)
    c: Horizontal(g3)
    c: Vertical(g0)
    c: Vertical(g2)
    c: Symmetric(g1,g0,g4)
    c: PointOnObject(g4,g-2)
    c: Distance(g0) = 34
    c: PointOnObject(g-1,g1)
    c: Distance(g3) = 16.8
    c: Coincident(g5,g6)
    c: Coincident(g6,g7)
    c: Coincident(g7,g8)
    c: Coincident(g8,g5)
    c: Horizontal(g6)
    c: Horizontal(g8)
    c: Vertical(g5)
    c: Vertical(g7)
    c: Symmetric(g6,g5,g9)
    c: Distance(g6) = 13
    c: Distance(g5) = 57
    c: Distance(g9,g-1) = 32.2
    c: Coincident(g10,g11)
    c: Coincident(g11,g12)
    c: Coincident(g12,g13)
    c: Coincident(g13,g10)
    c: Horizontal(g11)
    c: Horizontal(g13)
    c: Vertical(g10)
    c: Vertical(g12)
    c: Symmetric(g11,g10,g14)
    c: PointOnObject(g14,g-2)
    c: PointOnObject(g11,g-1)
    c: Distance(g12,g-2) = 22.1
    c: Distance(g10) = 68.9
    c: Coincident(g15,g16)
    c: Coincident(g16,g17)
    c: Coincident(g17,g18)
    c: Coincident(g18,g15)
    c: Horizontal(g16)
    c: Horizontal(g18)
    c: Vertical(g15)
    c: Vertical(g17)
    c: Symmetric(g16,g15,g19)
    c: PointOnObject(g19,g-2)
    c: Distance(g18) = 17
    c: Distance(g15) = 17
    c: Distance(g19,g-1) = 45.4
    c: Distance(g9,g-2) = 15.6
    c: Coincident(g20,g21)
    c: Coincident(g21,g22)
    c: Coincident(g22,g23)
    c: Coincident(g23,g20)
    c: Vertical(g20)
    c: Vertical(g22)
    c: Horizontal(g21)
    c: Horizontal(g23)
    c: PointOnObject(g20,g11)
    c: PointOnObject(g21,g10)
    c: Distance(g2,g20) = 0.3
FEATURE [PartDesign::Pocket] Pocket007  label="基板部2"
  BaseFeature = -> Pocket001
  Direction = (0,0,-1)
  Length = 4.5
  Length2 = 5
  Profile = -> Sketch018
  ReferenceAxis = -> Sketch018 [N_Axis]
  Refine = true
  Reversed = true
  SideType = 0
  Suppressed = false
  Type = 0
  Type2 = 0
FEATURE [PartDesign::Pocket] Pocket002  label="電池部"
  BaseFeature = -> Pocket007
  Direction = (0,1,-2e-16)
  Length = 54.1
  Length2 = 5
  Profile = -> Sketch008
  ReferenceAxis = -> Sketch008 [N_Axis]
  Reversed = true
  SideType = 0
  Suppressed = false
  Type = 0
  Type2 = 0
  expr: Length = Spreadsheet.battery_l + 0.3 * 2 - 3.5
FEATURE [PartDesign::Pocket] Pocket004  label="コネクタ部"
  BaseFeature = -> Pocket002
  Direction = (0,1,-2e-16)
  Length = 5
  Length2 = 5
  Profile = -> Sketch011
  ReferenceAxis = -> Sketch011 [N_Axis]
  SideType = 0
  Suppressed = false
  Type = 0
  Type2 = 0
FEATURE [PartDesign::Pocket] Pocket006  label="外形カット"
  BaseFeature = -> Pocket004
  Direction = (0,1,-2e-16)
  Length = 100
  Length2 = 100
  Profile = -> Sketch016
  ReferenceAxis = -> Sketch016 [N_Axis]
  SideType = 1
  Suppressed = false
  Type = 0
  Type2 = 0
FEATURE [PartDesign::Fillet] Fillet001
  Base = -> Pocket006 [Edge7,Face1,Edge12,Edge17,Edge24,Edge66,Edge25,Edge22,Edge31,Edge13,Edge18]
  BaseFeature = -> Pocket006
  Radius = 1
  Refine = true
  SupportTransform = false
  Suppressed = false
  UseAllEdges = false
FEATURE [PartDesign::Pad] Pad005  label="固定柱1"
  BaseFeature = -> Fillet001
  Direction = (0,0,1)
  Length = 2.1
  Length2 = 10
  Profile = -> Sketch012
  ReferenceAxis = -> Sketch012 [N_Axis]
  Reversed = true
  SideType = 1
  Suppressed = false
  Type = 0
  Type2 = 0
FEATURE [PartDesign::Pad] Pad006  label="固定柱2"
  BaseFeature = -> Pad005
  Direction = (0,0,1)
  Length = 4.5
  Length2 = 10
  Profile = -> Sketch014
  ReferenceAxis = -> Sketch014 [N_Axis]
  SideType = 0
  Suppressed = false
  Type = 0
  Type2 = 0
FEATURE [PartDesign::Chamfer] Chamfer001  label="固定柱面取り"
  Angle = 45
  Base = -> Pad006 [Face68]
  BaseFeature = -> Pad006
  ChamferType = 0
  FlipDirection = false
  Size = 0.5
  Size2 = 1
  SupportTransform = false
  Suppressed = false
  UseAllEdges = false
FEATURE [PartDesign::Pocket] Pocket005  label="電池ピン穴"
  BaseFeature = -> Chamfer001
  Direction = (0,0,-1)
  Length = 2.2
  Length2 = 5
  Profile = -> Sketch013
  ReferenceAxis = -> Sketch013 [N_Axis]
  Reversed = true
  SideType = 0
  Suppressed = false
  Type = 0
  Type2 = 0
FEATURE [Sketcher::SketchObject] Sketch019
  ArcFitTolerance = 1e-06
  AttachmentOffset = pos=(0,0,-1.6) rot=(0,0,1;0rad)
  AttachmentSupport = -> [XY_Plane]
  ExternalTypes = [0]
  FullyConstrained = false
  MakeInternals = false
  MapMode = 5
  Placement = pos=(0,0,-1.6) rot=(0,0,1;0rad)
  _ExternalGeoVersion = 0
  expr: Constraints[10] = Sketch017.Constraints[10]
  expr: Constraints[12] = Sketch017.Constraints[12]
  expr: Constraints[22] = Sketch017.Constraints[22]
  expr: Constraints[23] = Sketch017.Constraints[23]
  expr: Constraints[24] = Sketch017.Constraints[24]
  expr: Constraints[31] = Sketch017.Constraints[31]
  expr: Constraints[42] = Sketch017.Constraints[42]
  expr: Constraints[43] = Sketch017.Constraints[43]
  expr: Constraints[44] = Sketch017.Constraints[44]
  expr: Constraints[45] = Sketch017.Constraints[45]
  expr: Constraints[54] = Sketch017.Constraints[54]
  expr: Constraints[55] = Sketch017.Constraints[55]
  expr: Constraints[56] = Sketch017.Constraints[56]
  expr: Constraints[57] = Sketch017.Constraints[57]
  expr: Constraints[75] = Sketch017.Constraints[75]
  expr: Constraints[76] = Sketch017.Constraints[76]
  expr: Constraints[77] = Sketch017.Constraints[77]
  expr: Constraints[78] = Sketch017.Constraints[78]
  sketch-geometry (30):
    g0: LineSegment [constr] StartX=8.4 StartY=-34 StartZ=0 EndX=8.4 EndY=0 EndZ=0
    g1: LineSegment [constr] StartX=8.4 StartY=0 StartZ=0 EndX=-8.4 EndY=0 EndZ=0
    g2: LineSegment [constr] StartX=-8.4 StartY=0 StartZ=0 EndX=-8.4 EndY=-34 EndZ=0
    g3: LineSegment [constr] StartX=-8.4 StartY=-34 StartZ=0 EndX=8.4 EndY=-34 EndZ=0
    g4: GeomPoint [constr] X=0 Y=-17 Z=0
    g5: LineSegment [constr] StartX=-22.1 StartY=-60.7 StartZ=0 EndX=-22.1 EndY=-3.7 EndZ=0
    g6: LineSegment [constr] StartX=-22.1 StartY=-3.7 StartZ=0 EndX=-9.1 EndY=-3.7 EndZ=0
    g7: LineSegment [constr] StartX=-9.1 StartY=-3.7 StartZ=0 EndX=-9.1 EndY=-60.7 EndZ=0
    g8: LineSegment [constr] StartX=-9.1 StartY=-60.7 StartZ=0 EndX=-22.1 EndY=-60.7 EndZ=0
    g9: GeomPoint [constr] X=-15.6 Y=-32.2 Z=0
    g10: LineSegment [constr] StartX=21.5 StartY=-68.9 StartZ=0 EndX=21.5 EndY=0 EndZ=0
    g11: LineSegment [constr] StartX=21.5 StartY=0 StartZ=0 EndX=-21.5 EndY=0 EndZ=0
    g12: GeomPoint [constr] X=0 Y=-34.45 Z=0
    g13: LineSegment [constr] StartX=8.5 StartY=-53.9 StartZ=0 EndX=8.5 EndY=-36.9 EndZ=0
    g14: LineSegment [constr] StartX=8.5 StartY=-36.9 StartZ=0 EndX=-8.5 EndY=-36.9 EndZ=0
    g15: LineSegment [constr] StartX=-8.5 StartY=-36.9 StartZ=0 EndX=-8.5 EndY=-53.9 EndZ=0
    g16: LineSegment [constr] StartX=-8.5 StartY=-53.9 StartZ=0 EndX=8.5 EndY=-53.9 EndZ=0
    g17: GeomPoint [constr] X=0 Y=-45.4 Z=0
    g18: LineSegment [constr] StartX=-18.1 StartY=-59.7 StartZ=0 EndX=-24.1 EndY=-59.7 EndZ=0
    g19: LineSegment [constr] StartX=-24.1 StartY=-59.7 StartZ=0 EndX=-24.1 EndY=-64.7 EndZ=0
    g20: LineSegment [constr] StartX=-24.1 StartY=-64.7 StartZ=0 EndX=-18.1 EndY=-64.7 EndZ=0
    g21: LineSegment [constr] StartX=-18.1 StartY=-64.7 StartZ=0 EndX=-18.1 EndY=-59.7 EndZ=0
    g22: LineSegment [constr] StartX=-24.1 StartY=-3.3 StartZ=0 EndX=-24.1 EndY=-59.7 EndZ=0
    g23: LineSegment [constr] StartX=-18.1 StartY=-3.3 StartZ=0 EndX=-18.1 EndY=-59.7 EndZ=0
    g24: LineSegment [constr] StartX=-24.1 StartY=-59.7 StartZ=0 EndX=-22.2801 EndY=-64.7 EndZ=0
    g25: LineSegment [constr] StartX=-18.1 StartY=-64.7 StartZ=0 EndX=-22.2801 EndY=-64.7 EndZ=0
    g26: LineSegment StartX=5 StartY=0 StartZ=0 EndX=5 EndY=-1.2 EndZ=0
    g27: LineSegment StartX=5 StartY=-1.2 StartZ=0 EndX=9 EndY=-1.2 EndZ=0
    g28: LineSegment StartX=9 StartY=-1.2 StartZ=0 EndX=9 EndY=0 EndZ=0
    g29: LineSegment StartX=9 StartY=0 StartZ=0 EndX=5 EndY=0 EndZ=0
  constraints (79):
    c: Coincident(g0,g1)
    c: Coincident(g1,g2)
    c: Coincident(g2,g3)
    c: Coincident(g3,g0)
    c: Horizontal(g1)
    c: Horizontal(g3)
    c: Vertical(g0)
    c: Vertical(g2)
    c: Symmetric(g1,g0,g4)
    c: PointOnObject(g4,g-2)
    c: Distance(g0) = 34
    c: PointOnObject(g-1,g1)
    c: Distance(g3) = 16.8
    c: Coincident(g5,g6)
    c: Coincident(g6,g7)
    c: Coincident(g7,g8)
    c: Coincident(g8,g5)
    c: Horizontal(g6)
    c: Horizontal(g8)
    c: Vertical(g5)
    c: Vertical(g7)
    c: Symmetric(g6,g5,g9)
    c: Distance(g6) = 13
    c: Distance(g5) = 57
    c: Distance(g9,g-1) = 32.2
    c: Coincident(g10,g11)
    c: Horizontal(g11)
    c: Vertical(g10)
    c: Symmetric(g11,g10,g12)
    c: PointOnObject(g12,g-2)
    c: PointOnObject(g11,g-1)
    c: Distance(g10) = 68.9
    c: Coincident(g13,g14)
    c: Coincident(g14,g15)
    c: Coincident(g15,g16)
    c: Coincident(g16,g13)
    c: Horizontal(g14)
    c: Horizontal(g16)
    c: Vertical(g13)
    c: Vertical(g15)
    c: Symmetric(g14,g13,g17)
    c: PointOnObject(g17,g-2)
    c: Distance(g16) = 17
    c: Distance(g13) = 17
    c: Distance(g17,g-1) = 45.4
    c: Distance(g9,g-2) = 15.6
    c: Coincident(g18,g19)
    c: Coincident(g19,g20)
    c: Coincident(g20,g21)
    c: Coincident(g21,g18)
    c: Horizontal(g18)
    c: Horizontal(g20)
    c: Vertical(g19)
    c: Vertical(g21)
    c: Distance(g18,g8) = 1
    c: Distance(g19) = 5
    c: Distance(g20) = 6
    c: Distance(g20,g-2) = 18.1
    c: Coincident(g22,g18)
    c: Vertical(g22)
    c: Coincident(g23,g18)
    c: Vertical(g23)
    c: Coincident(g24,g18)
    c: PointOnObject(g24,g20)
    c: Coincident(g25,g20)
    c: Coincident(g25,g24)
    c: Coincident(g26,g27)
    c: Coincident(g27,g28)
    c: Coincident(g28,g29)
    c: Coincident(g29,g26)
    c: Vertical(g26)
    c: Vertical(g28)
    c: Horizontal(g27)
    c: Horizontal(g29)
    c: PointOnObject(g26,g1)
    c: DistanceX(g27,g27) = 4
    c: DistanceY(g28,g28) = 1.2
    c: DistanceX(g-1,g26) = 5
    c: Angle(g25,g24) = 1.91986
FEATURE [PartDesign::Pad] Pad009
  BaseFeature = -> Pocket005
  Direction = (0,0,1)
  Length = 2.3
  Length2 = 10
  Profile = -> Sketch019
  ReferenceAxis = -> Sketch019 [N_Axis]
  Refine = true
  Reversed = true
  SideType = 0
  Suppressed = false
  Type = 0
  Type2 = 0
FEATURE [PartDesign::Pad] Pad008  label="固定爪1"
  BaseFeature = -> Pad009
  Direction = (0,0,1)
  Length = 2
  Length2 = 10
  Profile = -> Sketch017
  ReferenceAxis = -> Sketch017 [N_Axis]
  Reversed = true
  SideType = 0
  Suppressed = false
  Type = 0
  Type2 = 0
FEATURE [PartDesign::Chamfer] Chamfer  label="固定爪1_逃げ"
  Angle = 45
  Base = -> Pad008 [Edge244]
  BaseFeature = -> Pad008
  ChamferType = 0
  FlipDirection = false
  Size = 0.9
  Size2 = 1
  SupportTransform = false
  Suppressed = false
  UseAllEdges = false
FEATURE [PartDesign::Body] Body
  AllowCompound = false
  Group = -> [Sketch,Sketch001,Sketch002,Pad,Sketch003,Pocket,Sketch007,Pocket001,Sketch008,Sketch018,Pocket007,Pocket002,Sketch011,Pocket004,Pocket006,Sketch012,Fillet001,Pad005,Sketch013,Sketch014,Pad006,Chamfer001,Pocket005,Sketch016,Sketch017,Sketch019,Pad009,Pad008,Chamfer]
  Origin = -> Origin
  Tip = -> Chamfer
COMPONENT P1 — recipe-attached ("Body003", modeled in this document).
Construction recipe (the document's own serialized feature program — sketch geometry with constraints, then the solid features built on it; lengths are millimeters unless a unit is written):

FEATURE [PartDesign::AdditiveSphere] Sphere
  Angle1 = -90
  Angle2 = 90
  Angle3 = 360
  AttacherType = Attacher::AttachEngine3D
  Radius = 12.5
  Refine = true
  Suppressed = false
FEATURE [PartDesign::Body] Body003
  AllowCompound = false
  Group = -> [Sphere]
  Origin = -> Origin006
  Placement = pos=(37,-63.6,8.7) rot=(0,0,1;0rad)
  Tip = -> Sphere
